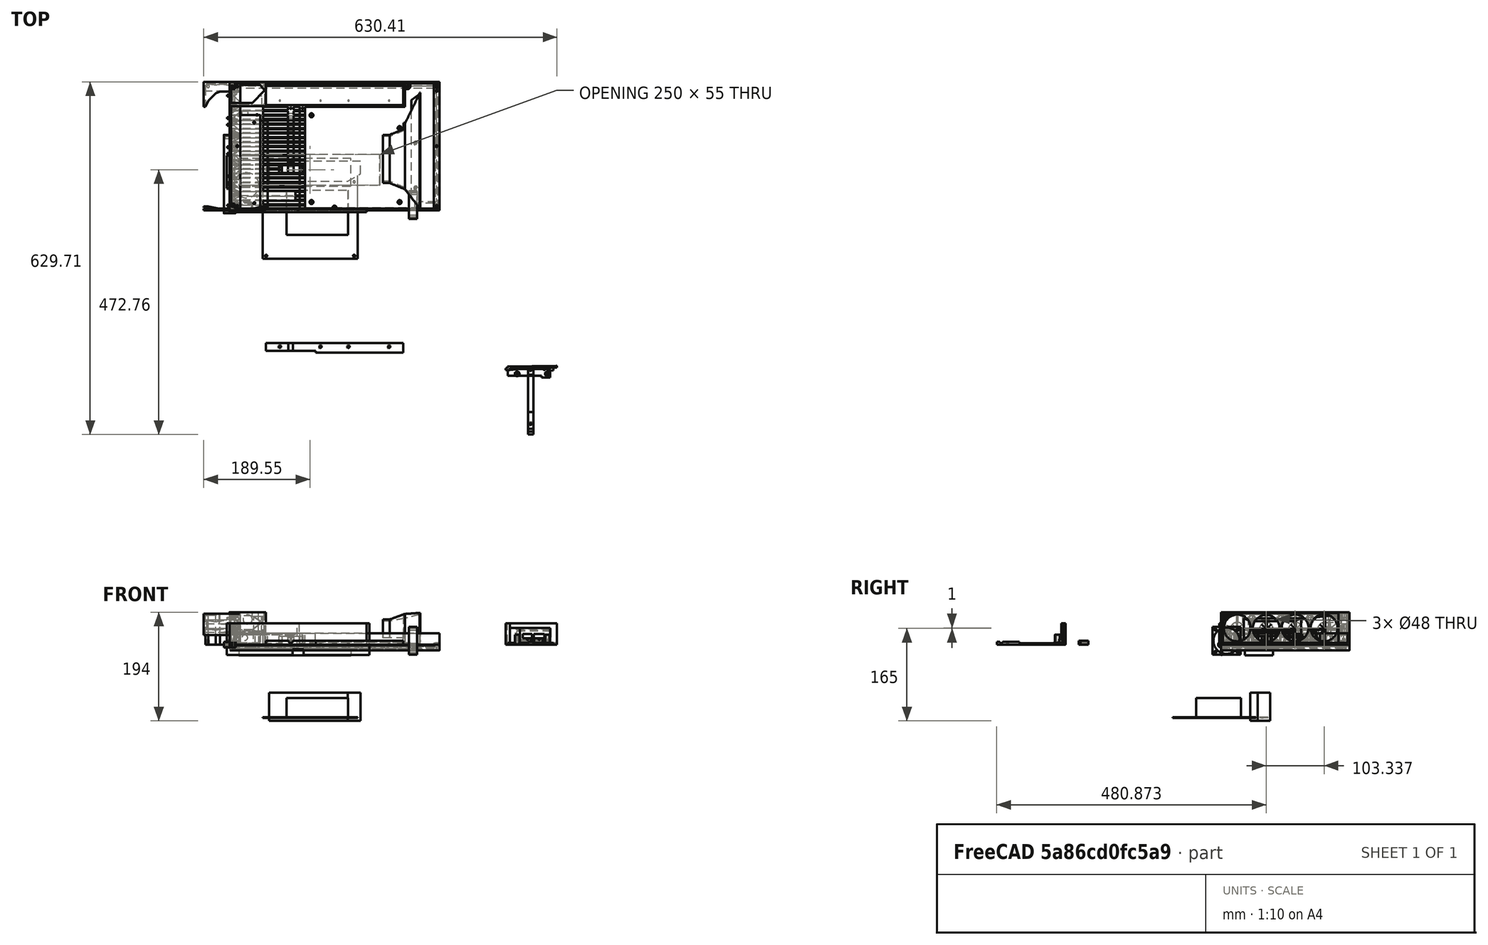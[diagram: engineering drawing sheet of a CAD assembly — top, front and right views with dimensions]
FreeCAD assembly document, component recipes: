
FREECAD ASSEMBLY — COMPONENT RECIPES ("4_fan_duct_version")

This assembly document has 13 components, labeled P0..P12 below (a component is one placed body or linked part). 13 of them carry a construction recipe — the FreeCAD feature program that regenerates the part from scratch, quoted from this document or its linked companion documents; the rest are supplied as boundary geometry only. No exploded tour is included for this assembly.
NOTE — this tour is split across 2 documents so each fits a 32k-token context. This is document 1: the component sections continue in the remaining 1 document, each repeating the header above.
COMPONENT P0 — recipe-attached ("BASE001", modeled in this document).
Construction recipe (the document's own serialized feature program — sketch geometry with constraints, then the solid features built on it; lengths are millimeters unless a unit is written):

FEATURE [Sketcher::SketchObject] Sketch014
  ArcFitTolerance = 1e-06
  AttachmentSupport = -> [XY_Plane013]
  FullyConstrained = true
  MakeInternals = false
  MapMode = 5
  expr: Constraints[20] = <<components>>.frame_w
  expr: Constraints[21] = <<components>>.frame_h
  expr: Constraints[22] = <<choices>>.corner
  expr: Constraints[25] = <<choices>>.shroud_base_screw_x
  expr: Constraints[26] = <<choices>>.shroud_base_screw_y2
  expr: Constraints[30] = <<choices>>.shroud_base_screw_y1
  expr: Constraints[31] = <<components>>.m3_threadhole
  expr: Constraints[33] = <<components>>.m3_hole
  expr: Constraints[34] = <<components>>.frame_w / 2
  sketch-geometry (14):
    g0: LineSegment StartX=1 StartY=0 StartZ=0 EndX=374 EndY=0 EndZ=0
    g1: LineSegment StartX=375 StartY=1 StartZ=0 EndX=375 EndY=228.5 EndZ=0
    g2: LineSegment StartX=374 StartY=229.5 StartZ=0 EndX=1 EndY=229.5 EndZ=0
    g3: LineSegment StartX=0 StartY=228.5 StartZ=0 EndX=0 EndY=1 EndZ=0
    g4: ArcOfCircle CenterX=1 CenterY=1 CenterZ=0 NormalX=0 NormalY=0 NormalZ=1 AngleXU=0 Radius=1 StartAngle=3.14159 EndAngle=4.71239
    g5: ArcOfCircle CenterX=374 CenterY=1 CenterZ=0 NormalX=0 NormalY=0 NormalZ=1 AngleXU=0 Radius=1 StartAngle=4.71239 EndAngle=6.28319
    g6: ArcOfCircle CenterX=374 CenterY=228.5 CenterZ=0 NormalX=0 NormalY=0 NormalZ=1 AngleXU=0 Radius=1 StartAngle=1.7e-15 EndAngle=1.5708
    g7: ArcOfCircle CenterX=1 CenterY=228.5 CenterZ=0 NormalX=0 NormalY=0 NormalZ=1 AngleXU=0 Radius=1 StartAngle=1.5708 EndAngle=3.14159
    g8: GeomPoint [constr] X=0 Y=0 Z=0
    g9: GeomPoint [constr] X=375 Y=229.5 Z=0
    g10: LineSegment [constr] StartX=332.5 StartY=0 StartZ=0 EndX=332.5 EndY=120 EndZ=0
    g11: Circle CenterX=332.5 CenterY=120 CenterZ=0 NormalX=0 NormalY=0 NormalZ=1 AngleXU=0 Radius=1.25
    g12: Circle CenterX=332.5 CenterY=40 CenterZ=0 NormalX=0 NormalY=0 NormalZ=1 AngleXU=0 Radius=1.25
    g13: Circle CenterX=187.5 CenterY=5 CenterZ=0 NormalX=0 NormalY=0 NormalZ=1 AngleXU=0 Radius=1.75
  constraints (35):
    c: Tangent(g0,g4) = -1.5708
    c: Tangent(g0,g5) = -1.5708
    c: Tangent(g1,g5) = -1.5708
    c: Tangent(g1,g6) = -1.5708
    c: Tangent(g2,g6) = -1.5708
    c: Tangent(g2,g7) = -1.5708
    c: Tangent(g3,g7) = -1.5708
    c: Tangent(g3,g4) = -1.5708
    c: Horizontal(g0)
    c: Horizontal(g2)
    c: Vertical(g1)
    c: Vertical(g3)
    c: Equal(g4,g5)
    c: Equal(g5,g6)
    c: Equal(g6,g7)
    c: PointOnObject(g8,g0)
    c: PointOnObject(g8,g3)
    c: PointOnObject(g9,g1)
    c: PointOnObject(g9,g2)
    c: Coincident(g8,g-1)
    c: DistanceX(g9) = 375
    c: DistanceY(g9) = 229.5
    c: Radius(g5) = 1
    c: PointOnObject(g10,g0)
    c: Vertical(g10)
    c: DistanceX(g10) = 332.5
    c: DistanceY(g10) = 120
    c: Coincident(g11,g10)
    c: PointOnObject(g12,g10)
    c: Equal(g12,g11)
    c: DistanceY(g12) = 40
    c: Diameter(g11) = 2.5
    c: DistanceY(g13) = 5
    c: Diameter(g13) = 3.5
    c: DistanceX(g13) = 187.5
FEATURE [PartDesign::Pad] Pad011
  Direction = (0,0,1)
  Length = 1.5
  Length2 = 10
  Profile = -> Sketch014
  ReferenceAxis = -> Sketch014 [N_Axis]
  Refine = true
  Suppressed = false
  Type = 0
FEATURE [Sketcher::SketchObject] Sketch016  label="motherboard standoffs"
  ArcFitTolerance = 1e-06
  AttachmentSupport = -> [XY_Plane013]
  FullyConstrained = false
  MakeInternals = false
  MapMode = 5
  expr: Constraints[10] = <<components>>.frame_w
  expr: Constraints[21] = <<choices>>.shroud_mb_space + <<components>>.fan_w + <<choices>>.exit_w
  expr: Constraints[42] = <<components>>.m3_threadhole
  expr: Constraints[51] = <<choices>>.mb_front_edge_gap
  expr: Constraints[57] = <<components>>.frame_w / 2
  expr: Constraints[62] = <<choices>>.screwhole_edge_margin
  expr: Constraints[63] = <<components>>.m3_hole
  expr: Constraints[9] = <<components>>.frame_h
  sketch-geometry (25):
    g0: LineSegment [constr] StartX=0 StartY=0 StartZ=0 EndX=375 EndY=0 EndZ=0
    g1: LineSegment [constr] StartX=375 StartY=0 StartZ=0 EndX=375 EndY=229.5 EndZ=0
    g2: LineSegment [constr] StartX=375 StartY=229.5 StartZ=0 EndX=0 EndY=229.5 EndZ=0
    g3: LineSegment [constr] StartX=0 StartY=229.5 StartZ=0 EndX=0 EndY=0 EndZ=0
    g4: LineSegment [constr] StartX=140 StartY=180 StartZ=0 EndX=140 EndY=10 EndZ=0
    g5: LineSegment [constr] StartX=140 StartY=10 StartZ=0 EndX=310 EndY=10 EndZ=0
    g6: LineSegment [constr] StartX=310 StartY=10 StartZ=0 EndX=310 EndY=180 EndZ=0
    g7: LineSegment [constr] StartX=310 StartY=180 StartZ=0 EndX=140 EndY=180 EndZ=0
    g8: LineSegment [constr] StartX=146.35 StartY=169.84 StartZ=0 EndX=146.35 EndY=14.8997 EndZ=0
    g9: LineSegment [constr] StartX=146.35 StartY=14.8997 StartZ=0 EndX=303.65 EndY=14.8997 EndZ=0
    g10: LineSegment [constr] StartX=303.65 StartY=14.8997 StartZ=0 EndX=303.65 EndY=146.98 EndZ=0
    g11: LineSegment [constr] StartX=303.65 StartY=146.98 StartZ=0 EndX=146.35 EndY=146.98 EndZ=0
    g12: Circle CenterX=146.35 CenterY=169.84 CenterZ=0 NormalX=0 NormalY=0 NormalZ=1 AngleXU=0 Radius=1.25
    g13: Circle CenterX=303.65 CenterY=146.98 CenterZ=0 NormalX=0 NormalY=0 NormalZ=1 AngleXU=0 Radius=1.25
    g14: Circle CenterX=303.65 CenterY=14.8997 CenterZ=0 NormalX=0 NormalY=0 NormalZ=1 AngleXU=0 Radius=1.25
    g15: Circle CenterX=146.35 CenterY=14.8997 CenterZ=0 NormalX=0 NormalY=0 NormalZ=1 AngleXU=0 Radius=1.25
    g16: Circle CenterX=146.35 CenterY=169.84 CenterZ=0 NormalX=0 NormalY=0 NormalZ=1 AngleXU=0 Radius=3.5
    g17: Circle CenterX=303.65 CenterY=146.98 CenterZ=0 NormalX=0 NormalY=0 NormalZ=1 AngleXU=0 Radius=3.5
    g18: Circle CenterX=303.65 CenterY=14.8997 CenterZ=0 NormalX=0 NormalY=0 NormalZ=1 AngleXU=0 Radius=3.5
    g19: Circle CenterX=146.35 CenterY=14.8997 CenterZ=0 NormalX=0 NormalY=0 NormalZ=1 AngleXU=0 Radius=3.5
    g20: Circle CenterX=187.5 CenterY=5 CenterZ=0 NormalX=0 NormalY=0 NormalZ=1 AngleXU=0 Radius=1.75
    g21: ArcOfCircle CenterX=187.5 CenterY=5 CenterZ=0 NormalX=0 NormalY=0 NormalZ=1 AngleXU=0 Radius=3.5 StartAngle=2e-16 EndAngle=3.14609
    g22: LineSegment StartX=191 StartY=5 StartZ=0 EndX=191 EndY=0 EndZ=0
    g23: LineSegment StartX=184 StartY=4.98426 StartZ=0 EndX=184.022 EndY=0 EndZ=0
    g24: LineSegment StartX=184.022 StartY=0 StartZ=0 EndX=191 EndY=0 EndZ=0
  constraints (64):
    c: Coincident(g0,g1)
    c: Coincident(g1,g2)
    c: Coincident(g2,g3)
    c: Coincident(g3,g0)
    c: Horizontal(g0)
    c: Horizontal(g2)
    c: Vertical(g1)
    c: Vertical(g3)
    c: Coincident(g0,g-1)
    c: DistanceY(g1,g1) = 229.5
    c: DistanceX(g2,g2) = 375
    c: Coincident(g4,g5)
    c: Coincident(g5,g6)
    c: Coincident(g6,g7)
    c: Coincident(g7,g4)
    c: Vertical(g4)
    c: Vertical(g6)
    c: Horizontal(g5)
    c: Horizontal(g7)
    c: Distance(g4,g6) = 170
    c: Distance(g5,g7) = 170
    c: Distance(g5,g1) = 65
    c: Vertical(g8)
    c: Coincident(g8,g9)
    c: Horizontal(g9)
    c: Coincident(g9,g10)
    c: Vertical(g10)
    c: Coincident(g10,g11)
    c: PointOnObject(g11,g8)
    c: Horizontal(g11)
    c: Distance(g8,g5) = 4.8997
    c: Distance(g8,g4) = 6.35
    c: Distance(g9,g6) = 6.35
    c: Distance(g8,g7) = 10.16
    c: Distance(g8,g11) = 22.86
    c: Coincident(g12,g8)
    c: Coincident(g13,g10)
    c: Coincident(g14,g9)
    c: Coincident(g15,g8)
    c: Equal(g12,g15)
    c: Equal(g15,g13)
    c: Equal(g13,g14)
    c: Diameter(g12) = 2.5
    c: Diameter(g16) = 7
    c: Coincident(g16,g8)
    c: Coincident(g17,g10)
    c: Coincident(g18,g9)
    c: Coincident(g19,g8)
    c: Equal(g18,g19)
    c: Equal(g19,g17)
    c: Equal(g17,g16)
    c: Distance(g4,g0) = 10
    c: Tangent(g21,g22) = 1.5708
    c: Tangent(g21,g23) = -1.5708
    c: Coincident(g21,g20)
    c: Vertical(g22)
    c: Equal(g19,g21)
    c: DistanceX(g20) = 187.5
    c: Coincident(g24,g23)
    c: Coincident(g24,g22)
    c: Horizontal(g24)
    c: PointOnObject(g23,g0)
    c: DistanceY(g20) = 5
    c: Diameter(g20) = 3.5
FEATURE [PartDesign::Pad] Pad013  label="mb_standoffs"
  BaseFeature = -> Pad011
  Direction = (0,0,1)
  Length = 7.25
  Length2 = 10
  Profile = -> Sketch016
  ReferenceAxis = -> Sketch016 [N_Axis]
  Refine = true
  Suppressed = false
  Type = 0
  expr: Length = <<choices>>.base_under_mb_thickness + 6
FEATURE [Sketcher::SketchObject] Sketch017
  ArcFitTolerance = 1e-06
  AttachmentSupport = -> [XY_Plane013]
  FullyConstrained = false
  MakeInternals = false
  MapMode = 5
  expr: Constraints[121] = <<choices>>.corner
  expr: Constraints[17] = <<components>>.fan_w + <<choices>>.exit_w + <<choices>>.shroud_mb_space + <<components>>.mb_w + 5
  expr: Constraints[31] = <<components>>.frame_h
  expr: Constraints[37] = <<choices>>.corner
  expr: Constraints[45] = <<choices>>.corner
  expr: Constraints[8] = <<components>>.frame_w
  expr: Constraints[9] = <<choices>>.mb_front_edge_gap + 170 + 5 + 3
  sketch-geometry (57):
    g0: LineSegment [constr] StartX=0 StartY=0 StartZ=0 EndX=375 EndY=0 EndZ=0
    g1: LineSegment [constr] StartX=375 StartY=0 StartZ=0 EndX=375 EndY=188 EndZ=0
    g2: LineSegment [constr] StartX=375 StartY=188 StartZ=0 EndX=0 EndY=188 EndZ=0
    g3: LineSegment [constr] StartX=0 StartY=188 StartZ=0 EndX=0 EndY=0 EndZ=0
    g4: LineSegment StartX=1 StartY=0 StartZ=0 EndX=374 EndY=0 EndZ=0
    g5: LineSegment StartX=375 StartY=1 StartZ=0 EndX=375 EndY=3 EndZ=0
    g6: LineSegment StartX=375 StartY=3 StartZ=0 EndX=135 EndY=3 EndZ=0
    g7: ArcOfCircle CenterX=1 CenterY=1 CenterZ=0 NormalX=0 NormalY=0 NormalZ=1 AngleXU=0 Radius=1 StartAngle=3.14159 EndAngle=4.71239
    g8: GeomPoint [constr] X=0 Y=0 Z=0
    g9: GeomPoint [constr] X=0 Y=188 Z=0
    g10: ArcOfCircle CenterX=374 CenterY=1 CenterZ=0 NormalX=0 NormalY=0 NormalZ=1 AngleXU=0 Radius=1 StartAngle=4.71239 EndAngle=6.28319
    g11: GeomPoint [constr] X=375 Y=0 Z=0
    g12: LineSegment StartX=375 StartY=228.5 StartZ=0 EndX=375 EndY=226.5 EndZ=0
    g13: LineSegment [constr] StartX=2 StartY=221.5 StartZ=0 EndX=2 EndY=192.907 EndZ=0
    g14: ArcOfCircle CenterX=1 CenterY=228.5 CenterZ=0 NormalX=0 NormalY=0 NormalZ=1 AngleXU=0 Radius=1 StartAngle=1.5708 EndAngle=3.14159
    g15: GeomPoint [constr] X=0 Y=229.5 Z=0
    g16: ArcOfCircle [constr] CenterX=7 CenterY=221.5 CenterZ=0 NormalX=0 NormalY=0 NormalZ=1 AngleXU=0 Radius=5 StartAngle=1.5708 EndAngle=3.14159
    g17: GeomPoint [constr] X=2 Y=226.5 Z=0
    g18: ArcOfCircle CenterX=374 CenterY=228.5 CenterZ=0 NormalX=0 NormalY=0 NormalZ=1 AngleXU=0 Radius=1 StartAngle=5.5e-15 EndAngle=1.5708
    g19: GeomPoint [constr] X=375 Y=229.5 Z=0
    g20: ArcOfCircle [constr] CenterX=7 CenterY=192.907 CenterZ=0 NormalX=0 NormalY=0 NormalZ=1 AngleXU=0 Radius=5 StartAngle=3.14159 EndAngle=4.90523
    g21: GeomPoint [constr] X=2 Y=188 Z=0
    g22: LineSegment StartX=313 StartY=226.5 StartZ=0 EndX=313 EndY=185 EndZ=0
    g23: LineSegment StartX=313 StartY=185 StartZ=0 EndX=310 EndY=185 EndZ=0
    g24: LineSegment StartX=310 StartY=185 StartZ=0 EndX=310 EndY=226.5 EndZ=0
    g25: LineSegment StartX=375 StartY=226.5 StartZ=0 EndX=313 EndY=226.5 EndZ=0
    g26: LineSegment [constr] StartX=313 StartY=226.5 StartZ=0 EndX=310 EndY=226.5 EndZ=0
    g27: LineSegment StartX=1 StartY=229.5 StartZ=0 EndX=308.406 EndY=229.5 EndZ=0
    g28: LineSegment [constr] StartX=308.406 StartY=229.5 StartZ=0 EndX=310 EndY=229.5 EndZ=0
    g29: LineSegment StartX=310 StartY=229.5 StartZ=0 EndX=374 EndY=229.5 EndZ=0
    g30: LineSegment [constr] StartX=310 StartY=226.5 StartZ=0 EndX=307.803 EndY=226.5 EndZ=0
    g31: LineSegment StartX=308.406 StartY=229.5 StartZ=0 EndX=307.803 EndY=226.5 EndZ=0
    g32: LineSegment StartX=310 StartY=229.5 StartZ=0 EndX=310 EndY=226.5 EndZ=0
    g33: LineSegment StartX=58 StartY=226.5 StartZ=0 EndX=7 EndY=226.5 EndZ=0
    g34: LineSegment StartX=307.803 StartY=226.5 StartZ=0 EndX=65 EndY=226.5 EndZ=0
    g35: LineSegment [constr] StartX=65 StartY=226.5 StartZ=0 EndX=63 EndY=226.5 EndZ=0
    g36: LineSegment StartX=58 StartY=188 StartZ=0 EndX=7.95824 EndY=188 EndZ=0
    g37: LineSegment StartX=135 StartY=188 StartZ=0 EndX=65 EndY=188 EndZ=0
    g38: LineSegment [constr] StartX=65 StartY=188 StartZ=0 EndX=63 EndY=188 EndZ=0
    g39: LineSegment StartX=63 StartY=221.5 StartZ=0 EndX=63 EndY=193 EndZ=0
    g40: LineSegment StartX=65 StartY=188 StartZ=0 EndX=65 EndY=226.5 EndZ=0
    g41: ArcOfCircle CenterX=58 CenterY=193 CenterZ=0 NormalX=0 NormalY=0 NormalZ=1 AngleXU=0 Radius=5 StartAngle=4.71239 EndAngle=6.28319
    g42: GeomPoint [constr] X=63 Y=188 Z=0
    g43: ArcOfCircle CenterX=58 CenterY=221.5 CenterZ=0 NormalX=0 NormalY=0 NormalZ=1 AngleXU=0 Radius=5 StartAngle=1.3e-15 EndAngle=1.5708
    g44: GeomPoint [constr] X=63 Y=226.5 Z=0
    g45: LineSegment StartX=135 StartY=3 StartZ=0 EndX=135 EndY=185 EndZ=0
    g46: LineSegment [constr] StartX=135 StartY=185 StartZ=0 EndX=135 EndY=188 EndZ=0
    g47: LineSegment StartX=135 StartY=188 StartZ=0 EndX=152 EndY=188 EndZ=0
    g48: LineSegment StartX=153 StartY=187 StartZ=0 EndX=153 EndY=185 EndZ=0
    g49: LineSegment StartX=153 StartY=185 StartZ=0 EndX=135 EndY=185 EndZ=0
    g50: ArcOfCircle CenterX=152 CenterY=187 CenterZ=0 NormalX=0 NormalY=0 NormalZ=1 AngleXU=0 Radius=1 StartAngle=1e-14 EndAngle=1.5708
    g51: GeomPoint [constr] X=153 Y=188 Z=0
    g52: LineSegment StartX=0 StartY=228.5 StartZ=0 EndX=0 EndY=226.5 EndZ=0
    g53: LineSegment [constr] StartX=0 StartY=226.5 StartZ=0 EndX=0 EndY=188 EndZ=0
    g54: LineSegment StartX=0 StartY=188 StartZ=0 EndX=-6e-16 EndY=1 EndZ=0
    g55: LineSegment StartX=0 StartY=226.5 StartZ=0 EndX=7 EndY=226.5 EndZ=0
    g56: LineSegment StartX=0 StartY=188 StartZ=0 EndX=7.95824 EndY=188 EndZ=0
  constraints (135):
    c: Coincident(g0,g1)
    c: Coincident(g2,g3)
    c: Coincident(g3,g0)
    c: Horizontal(g0)
    c: Horizontal(g2)
    c: Vertical(g1)
    c: Vertical(g3)
    c: Coincident(g0,g-1)
    c: DistanceX(g2,g2) = 375
    c: DistanceY(g1,g1) = 188
    c: Coincident(g9,g2)
    c: Coincident(g8,g0)
    c: Coincident(g11,g0)
    c: PointOnObject(g5,g1)
    c: Coincident(g5,g6)
    c: Horizontal(g6)
    c: Coincident(g6,g45)
    c: Distance(g6,g1) = 240
    c: PointOnObject(g8,g4)
    c: Tangent(g4,g7) = -1.5708
    c: Coincident(g54,g7) = -1.5708
    c: PointOnObject(g11,g5)
    c: PointOnObject(g11,g4)
    c: Tangent(g5,g10) = -1.5708
    c: Tangent(g4,g10) = -1.5708
    c: PointOnObject(g46,g2)
    c: Coincident(g37,g46)
    c: Radius(g10) = 1
    c: Coincident(g2,g1)
    c: DistanceY(g6) = 3
    c: DistanceX(g21) = 2
    c: DistanceY(g15) = 229.5
    c: Coincident(g12,g25)
    c: Vertical(g13)
    c: Coincident(g52,g14) = -1.5708
    c: Coincident(g27,g14) = 1.5708
    c: Equal(g14,g7)
    c: Radius(g7) = 1
    c: PointOnObject(g17,g13)
    c: Tangent(g13,g16) = -1.5708
    c: Vertical(g12)
    c: PointOnObject(g12,g1)
    c: PointOnObject(g19,g12)
    c: Coincident(g29,g18) = 1.5708
    c: Tangent(g12,g18) = 1.5708
    c: Radius(g18) = 1
    c: PointOnObject(g21,g13)
    c: Coincident(g36,g20) = 1.5708
    c: Tangent(g13,g20) = -1.5708
    c: Equal(g20,g16)
    c: Radius(g16) = 5
    c: Vertical(g22)
    c: Coincident(g22,g23)
    c: Horizontal(g23)
    c: Coincident(g23,g24)
    c: Vertical(g24)
    c: Coincident(g26,g30)
    c: Coincident(g25,g26)
    c: Horizontal(g25)
    c: Horizontal(g26)
    c: PointOnObject(g17,g25)
    c: Coincident(g25,g22)
    c: Coincident(g30,g24)
    c: Distance(g22,g1) = 62
    c: Distance(g46,g23) = 3
    c: DistanceX(g23,g23) = 3
    c: Coincident(g27,g28)
    c: Horizontal(g27)
    c: Distance(g17,g27) = 3
    c: PointOnObject(g15,g27)
    c: PointOnObject(g19,g27)
    c: Coincident(g28,g29)
    c: Horizontal(g28)
    c: Horizontal(g29)
    c: Coincident(g30,g34)
    c: Horizontal(g30)
    c: Coincident(g31,g27)
    c: Coincident(g31,g30)
    c: Coincident(g32,g28)
    c: Coincident(g32,g24)
    c: Vertical(g32)
    c: Coincident(g35,g44)
    c: Horizontal(g33)
    c: Coincident(g34,g35)
    c: Horizontal(g34)
    c: Horizontal(g35)
    c: Coincident(g38,g42)
    c: Horizontal(g36)
    c: Coincident(g37,g38)
    c: Horizontal(g37)
    c: Horizontal(g38)
    c: PointOnObject(g21,g37)
    c: Vertical(g39)
    c: Coincident(g40,g37)
    c: Coincident(g40,g34)
    c: Vertical(g40)
    c: Distance(g42,g40) = 2
    c: DistanceX(g34) = 65
    c: PointOnObject(g42,g36)
    c: PointOnObject(g42,g39)
    c: Tangent(g36,g41) = 1.5708
    c: Tangent(g39,g41) = 1.5708
    c: PointOnObject(g44,g39)
    c: Tangent(g39,g43) = 1.5708
    c: Equal(g16,g43)
    c: Equal(g43,g41)
    c: Coincident(g45,g46)
    c: Vertical(g45)
    c: Vertical(g46)
    c: Coincident(g37,g47)
    c: PointOnObject(g51,g2)
    c: Vertical(g48)
    c: Coincident(g48,g49)
    c: Coincident(g49,g45)
    c: Horizontal(g49)
    c: DistanceY(g48,g51) = 3
    c: DistanceX(g47,g51) = 18
    c: PointOnObject(g51,g47)
    c: PointOnObject(g51,g48)
    c: Tangent(g47,g50) = 1.5708
    c: Tangent(g48,g50) = 1.5708
    c: Radius(g50) = 1
    c: Tangent(g43,g33) = -1.5708
    c: Tangent(g16,g33) = -1.5708
    c: Distance(g16,g27) = 3
    c: Coincident(g52,g53)
    c: PointOnObject(g8,g52)
    c: PointOnObject(g9,g52)
    c: PointOnObject(g15,g52)
    c: Coincident(g53,g54)
    c: Coincident(g55,g52)
    c: Tangent(g55,g16) = 1.5708
    c: Coincident(g56,g53)
    c: Coincident(g56,g20)
    c: Horizontal(g56)
FEATURE [PartDesign::Pad] Pad014  label="thick_area"
  BaseFeature = -> Pad013
  Direction = (0,0,1)
  Length = 20
  Length2 = 10
  Profile = -> Sketch017
  ReferenceAxis = -> Sketch017 [N_Axis]
  Refine = true
  Suppressed = false
  Type = 0
  expr: Length = <<choices>>.base_max_thickness
FEATURE [Sketcher::SketchObject] Sketch018
  ArcFitTolerance = 1e-06
  AttachmentSupport = -> [XY_Plane013]
  FullyConstrained = true
  MakeInternals = false
  MapMode = 5
  expr: Constraints[30] = <<components>>.m3_hole
  expr: Constraints[31] = <<choices>>.psu_left_gap
  sketch-geometry (14):
    g0: LineSegment [constr] StartX=60 StartY=183 StartZ=0 EndX=5 EndY=183 EndZ=0
    g1: LineSegment [constr] StartX=5 StartY=183 StartZ=0 EndX=5 EndY=13 EndZ=0
    g2: LineSegment [constr] StartX=5 StartY=13 StartZ=0 EndX=60 EndY=13 EndZ=0
    g3: LineSegment [constr] StartX=60 StartY=13 StartZ=0 EndX=60 EndY=183 EndZ=0
    g4: GeomPoint [constr] X=32.5 Y=98 Z=0
    g5: LineSegment [constr] StartX=49.15 StartY=170 StartZ=0 EndX=15.85 EndY=170 EndZ=0
    g6: LineSegment [constr] StartX=15.85 StartY=170 StartZ=0 EndX=15.85 EndY=26 EndZ=0
    g7: LineSegment [constr] StartX=15.85 StartY=26 StartZ=0 EndX=49.15 EndY=26 EndZ=0
    g8: LineSegment [constr] StartX=49.15 StartY=26 StartZ=0 EndX=49.15 EndY=170 EndZ=0
    g9: GeomPoint [constr] X=32.5 Y=98 Z=0
    g10: Circle CenterX=15.85 CenterY=170 CenterZ=0 NormalX=0 NormalY=0 NormalZ=1 AngleXU=0 Radius=1.75
    g11: Circle CenterX=49.15 CenterY=170 CenterZ=0 NormalX=0 NormalY=0 NormalZ=1 AngleXU=0 Radius=1.75
    g12: Circle CenterX=15.85 CenterY=26 CenterZ=0 NormalX=0 NormalY=0 NormalZ=1 AngleXU=0 Radius=1.75
    g13: Circle CenterX=49.15 CenterY=26 CenterZ=0 NormalX=0 NormalY=0 NormalZ=1 AngleXU=0 Radius=1.75
  constraints (33):
    c: Coincident(g0,g1)
    c: Coincident(g1,g2)
    c: Coincident(g2,g3)
    c: Coincident(g3,g0)
    c: Horizontal(g0)
    c: Horizontal(g2)
    c: Vertical(g1)
    c: Vertical(g3)
    c: Symmetric(g2,g0,g4)
    c: Coincident(g5,g6)
    c: Coincident(g6,g7)
    c: Coincident(g7,g8)
    c: Coincident(g8,g5)
    c: Horizontal(g5)
    c: Horizontal(g7)
    c: Vertical(g6)
    c: Vertical(g8)
    c: Symmetric(g7,g5,g9)
    c: Coincident(g9,g4)
    c: DistanceX(g5,g5) = 33.3
    c: DistanceY(g6,g6) = 144
    c: DistanceY(g1,g1) = 170
    c: DistanceX(g0,g0) = 55
    c: Coincident(g10,g5)
    c: Coincident(g11,g5)
    c: Coincident(g12,g6)
    c: Coincident(g13,g7)
    c: Equal(g10,g11)
    c: Equal(g11,g12)
    c: Equal(g12,g13)
    c: Diameter(g10) = 3.5
    c: DistanceX(g-2,g1) = 5
    c: DistanceY(g1) = 13
FEATURE [PartDesign::Pocket] Pocket004  label="psu_mounts"
  BaseFeature = -> Pad014
  Direction = (0,0,-1)
  Length = 5
  Length2 = 5
  Profile = -> Sketch018
  ReferenceAxis = -> Sketch018 [N_Axis]
  Refine = true
  Reversed = true
  Suppressed = false
  Type = 1
FEATURE [Sketcher::SketchObject] Sketch019
  ArcFitTolerance = 1e-06
  AttachmentSupport = -> [XY_Plane013]
  FullyConstrained = true
  MakeInternals = false
  MapMode = 5
  expr: Constraints[10] = <<components>>.frame_h
  expr: Constraints[20] = <<choices>>.mb_front_edge_gap + 170 + 5 + 3
  expr: Constraints[21] = <<choices>>.exit_w + <<components>>.fan_w + <<choices>>.shroud_mb_space
  expr: Constraints[9] = <<components>>.frame_w
  sketch-geometry (8):
    g0: LineSegment [constr] StartX=0 StartY=0 StartZ=0 EndX=375 EndY=0 EndZ=0
    g1: LineSegment [constr] StartX=375 StartY=0 StartZ=0 EndX=375 EndY=229.5 EndZ=0
    g2: LineSegment [constr] StartX=375 StartY=229.5 StartZ=0 EndX=0 EndY=229.5 EndZ=0
    g3: LineSegment [constr] StartX=0 StartY=229.5 StartZ=0 EndX=0 EndY=0 EndZ=0
    g4: LineSegment StartX=65 StartY=188 StartZ=0 EndX=310 EndY=188 EndZ=0
    g5: LineSegment StartX=310 StartY=188 StartZ=0 EndX=310 EndY=229.5 EndZ=0
    g6: LineSegment StartX=310 StartY=229.5 StartZ=0 EndX=65 EndY=229.5 EndZ=0
    g7: LineSegment StartX=65 StartY=229.5 StartZ=0 EndX=65 EndY=188 EndZ=0
  constraints (23):
    c: Coincident(g0,g1)
    c: Coincident(g1,g2)
    c: Coincident(g2,g3)
    c: Coincident(g3,g0)
    c: Horizontal(g0)
    c: Horizontal(g2)
    c: Vertical(g1)
    c: Vertical(g3)
    c: Coincident(g0,g-1)
    c: DistanceX(g2,g2) = 375
    c: DistanceY(g1,g1) = 229.5
    c: Coincident(g4,g5)
    c: Coincident(g5,g6)
    c: Coincident(g6,g7)
    c: Coincident(g7,g4)
    c: Horizontal(g4)
    c: Horizontal(g6)
    c: Vertical(g5)
    c: Vertical(g7)
    c: PointOnObject(g5,g2)
    c: Distance(g4,g0) = 188
    c: Distance(g4,g1) = 65
    c: DistanceX(g6) = 65
FEATURE [PartDesign::Pocket] Pocket005  label="back_hole"
  BaseFeature = -> Pocket004
  Direction = (0,0,-1)
  Length = 5
  Length2 = 5
  Profile = -> Sketch019
  ReferenceAxis = -> Sketch019 [N_Axis]
  Refine = true
  Reversed = true
  Suppressed = false
  Type = 1
FEATURE [Sketcher::SketchObject] Sketch020
  ArcFitTolerance = 1e-06
  AttachmentSupport = -> [XY_Plane013]
  FullyConstrained = false
  MakeInternals = false
  MapMode = 5
  expr: Constraints[20] = <<choices>>.fin_gap
  expr: Constraints[21] = <<choices>>.fin_end
  expr: Constraints[9] = <<components>>.frame_h
  sketch-geometry (8):
    g0: LineSegment [constr] StartX=0 StartY=0 StartZ=0 EndX=125.373 EndY=0 EndZ=0
    g1: LineSegment [constr] StartX=125.373 StartY=0 StartZ=0 EndX=125.373 EndY=229.5 EndZ=0
    g2: LineSegment [constr] StartX=125.373 StartY=229.5 StartZ=0 EndX=0 EndY=229.5 EndZ=0
    g3: LineSegment [constr] StartX=0 StartY=229.5 StartZ=0 EndX=0 EndY=0 EndZ=0
    g4: LineSegment StartX=0 StartY=3 StartZ=0 EndX=125.373 EndY=3 EndZ=0
    g5: LineSegment StartX=125.373 StartY=3 StartZ=0 EndX=125.373 EndY=9 EndZ=0
    g6: LineSegment StartX=125.373 StartY=9 StartZ=0 EndX=0 EndY=9 EndZ=0
    g7: LineSegment StartX=0 StartY=9 StartZ=0 EndX=0 EndY=3 EndZ=0
  constraints (22):
    c: Coincident(g0,g1)
    c: Coincident(g1,g2)
    c: Coincident(g2,g3)
    c: Coincident(g3,g0)
    c: Horizontal(g0)
    c: Horizontal(g2)
    c: Vertical(g1)
    c: Vertical(g3)
    c: Coincident(g0,g-1)
    c: DistanceY(g1,g1) = 229.5
    c: Coincident(g4,g5)
    c: Coincident(g5,g6)
    c: Coincident(g6,g7)
    c: Coincident(g7,g4)
    c: Horizontal(g4)
    c: Horizontal(g6)
    c: Vertical(g5)
    c: Vertical(g7)
    c: PointOnObject(g4,g3)
    c: PointOnObject(g5,g1)
    c: DistanceY(g5,g5) = 6
    c: Distance(g4,g0) = 3
FEATURE [PartDesign::Pocket] Pocket006
  BaseFeature = -> Pocket005
  Direction = (0,0,-1)
  Length = 18
  Length2 = 5
  Profile = -> Sketch020
  ReferenceAxis = -> Sketch020 [N_Axis]
  Refine = true
  Reversed = true
  Suppressed = false
  Type = 0
  expr: Length = <<choices>>.base_max_thickness - 2
FEATURE [PartDesign::Plane] DatumPlane001  label="just_above_base_thinnest"
  AttachmentOffset = pos=(0,0,2) rot=(0,0,1;0rad)
  AttachmentSupport = -> [XY_Plane013]
  Length = 463.812
  MapMode = 5
  Placement = pos=(0,0,2) rot=(0,0,1;0rad)
  ResizeMode = 0
  Width = 318.312
FEATURE [Sketcher::SketchObject] Sketch021
  ArcFitTolerance = 1e-06
  AttachmentSupport = -> [DatumPlane001]
  FullyConstrained = true
  MakeInternals = false
  MapMode = 5
  Placement = pos=(0,0,2) rot=(0,0,1;0rad)
  expr: Constraints[19] = <<choices>>.fin_gap
  expr: Constraints[20] = <<choices>>.fin_end
  expr: Constraints[21] = <<choices>>.psu_left_gap + <<components>>.psu_w
  expr: Constraints[22] = <<components>>.frame_w - <<components>>.fan_w - <<choices>>.exit_w - <<choices>>.shroud_mb_space - 170 - 5
  expr: Constraints[9] = <<components>>.frame_h
  sketch-geometry (8):
    g0: LineSegment [constr] StartX=0 StartY=0 StartZ=0 EndX=135 EndY=0 EndZ=0
    g1: LineSegment [constr] StartX=135 StartY=0 StartZ=0 EndX=135 EndY=229.5 EndZ=0
    g2: LineSegment [constr] StartX=135 StartY=229.5 StartZ=0 EndX=0 EndY=229.5 EndZ=0
    g3: LineSegment [constr] StartX=0 StartY=229.5 StartZ=0 EndX=0 EndY=0 EndZ=0
    g4: LineSegment StartX=60 StartY=3 StartZ=0 EndX=135 EndY=3 EndZ=0
    g5: LineSegment StartX=135 StartY=3 StartZ=0 EndX=135 EndY=9 EndZ=0
    g6: LineSegment StartX=135 StartY=9 StartZ=0 EndX=60 EndY=9 EndZ=0
    g7: LineSegment StartX=60 StartY=9 StartZ=0 EndX=60 EndY=3 EndZ=0
  constraints (23):
    c: Coincident(g0,g1)
    c: Coincident(g1,g2)
    c: Coincident(g2,g3)
    c: Coincident(g3,g0)
    c: Horizontal(g0)
    c: Horizontal(g2)
    c: Vertical(g1)
    c: Vertical(g3)
    c: Coincident(g0,g-1)
    c: DistanceY(g1,g1) = 229.5
    c: Coincident(g4,g5)
    c: Coincident(g5,g6)
    c: Coincident(g6,g7)
    c: Coincident(g7,g4)
    c: Horizontal(g4)
    c: Horizontal(g6)
    c: Vertical(g5)
    c: Vertical(g7)
    c: PointOnObject(g5,g1)
    c: DistanceY(g5,g5) = 6
    c: Distance(g4,g0) = 3
    c: Distance(g4,g3) = 60
    c: DistanceX(g0) = 135
FEATURE [PartDesign::Pocket] Pocket007
  BaseFeature = -> Pocket006
  Direction = (0,0,-1)
  Length = 5
  Length2 = 5
  Profile = -> Sketch021
  ReferenceAxis = -> Sketch021 [N_Axis]
  Refine = true
  Reversed = true
  Suppressed = false
  Type = 1
FEATURE [PartDesign::LinearPattern] LinearPattern
  BaseFeature = -> Pocket007
  Direction = -> Sketch020 [V_Axis]
  Length = 176
  Mode = 1
  Occurrences = 23
  Offset = 8
  Originals = -> [Pocket006,Pocket007]
  Refine = true
  Suppressed = false
  TransformMode = 0
  expr: Occurrences = <<choices>>.fin_count + 1
  expr: Offset = <<choices>>.fin_thick + <<choices>>.fin_gap
FEATURE [Sketcher::SketchObject] Sketch035
  ArcFitTolerance = 1e-06
  AttachmentSupport = -> [XY_Plane013]
  FullyConstrained = false
  MakeInternals = false
  MapMode = 5
  expr: Constraints[10] = <<components>>.frame_w - 62
  expr: Constraints[8] = 170 + <<choices>>.mb_front_edge_gap + 5 + 3
  sketch-geometry (4):
    g0: LineSegment StartX=127.279 StartY=188 StartZ=0 EndX=127.279 EndY=185 EndZ=0
    g1: LineSegment StartX=127.279 StartY=185 StartZ=0 EndX=313 EndY=185 EndZ=0
    g2: LineSegment StartX=313 StartY=185 StartZ=0 EndX=313 EndY=188 EndZ=0
    g3: LineSegment StartX=313 StartY=188 StartZ=0 EndX=127.279 EndY=188 EndZ=0
  constraints (11):
    c: Coincident(g0,g1)
    c: Coincident(g1,g2)
    c: Coincident(g2,g3)
    c: Coincident(g3,g0)
    c: Vertical(g0)
    c: Vertical(g2)
    c: Horizontal(g1)
    c: Horizontal(g3)
    c: DistanceY(g0) = 188
    c: DistanceY(g0,g0) = 3
    c: DistanceX(g2) = 313
FEATURE [PartDesign::Pad] Pad020  label="lip in front of rear ports"
  BaseFeature = -> LinearPattern
  Direction = (0,0,1)
  Length = 4.25
  Length2 = 10
  Profile = -> Sketch035
  ReferenceAxis = -> Sketch035 [N_Axis]
  Refine = true
  Suppressed = false
  Type = 0
  expr: Length = 3 + <<choices>>.base_under_mb_thickness
FEATURE [Sketcher::SketchObject] Sketch045
  ArcFitTolerance = 1e-06
  AttachmentSupport = -> [XY_Plane013]
  FullyConstrained = false
  MakeInternals = false
  MapMode = 5
  expr: Constraints[19] = <<choices>>.corner
  expr: Constraints[26] = 3 + <<choices>>.screwhole_edge_margin
  expr: Constraints[29] = <<components>>.fan_w + <<choices>>.exit_w + <<choices>>.shroud_mb_space - <<choices>>.screwhole_edge_margin - 3
  expr: Constraints[39] = <<components>>.frame_h
  expr: Constraints[52] = <<choices>>.corner
  expr: Constraints[7] = <<choices>>.screwhole_edge_margin * 2
  expr: Constraints[8] = <<components>>.frame_h
  expr: Constraints[9] = <<components>>.frame_w
  sketch-geometry (21):
    g0: LineSegment StartX=365 StartY=0 StartZ=0 EndX=374 EndY=0 EndZ=0
    g1: LineSegment StartX=375 StartY=1 StartZ=0 EndX=375 EndY=228.5 EndZ=0
    g2: LineSegment StartX=374 StartY=229.5 StartZ=0 EndX=365 EndY=229.5 EndZ=0
    g3: LineSegment StartX=365 StartY=229.5 StartZ=0 EndX=365 EndY=0 EndZ=0
    g4: ArcOfCircle CenterX=374 CenterY=1 CenterZ=0 NormalX=0 NormalY=0 NormalZ=1 AngleXU=0 Radius=1 StartAngle=4.71239 EndAngle=6.28319
    g5: GeomPoint [constr] X=375 Y=0 Z=0
    g6: ArcOfCircle CenterX=374 CenterY=228.5 CenterZ=0 NormalX=0 NormalY=0 NormalZ=1 AngleXU=0 Radius=1 StartAngle=-3.6e-15 EndAngle=1.5708
    g7: GeomPoint [constr] X=375 Y=229.5 Z=0
    g8: LineSegment StartX=323 StartY=221.5 StartZ=0 EndX=323 EndY=228.5 EndZ=0
    g9: LineSegment StartX=323 StartY=228.5 StartZ=0 EndX=313 EndY=228.5 EndZ=0
    g10: LineSegment StartX=313 StartY=228.5 StartZ=0 EndX=313 EndY=221.5 EndZ=0
    g11: LineSegment StartX=0 StartY=228.5 StartZ=0 EndX=0 EndY=185.5 EndZ=0
    g12: LineSegment StartX=0 StartY=185.5 StartZ=0 EndX=10 EndY=185.5 EndZ=0
    g13: LineSegment StartX=10 StartY=185.5 StartZ=0 EndX=10 EndY=229.5 EndZ=0
    g14: LineSegment StartX=10 StartY=229.5 StartZ=0 EndX=1 EndY=229.5 EndZ=0
    g15: ArcOfCircle [constr] CenterX=318 CenterY=221.5 CenterZ=0 NormalX=0 NormalY=0 NormalZ=1 AngleXU=0 Radius=5 StartAngle=3.14159 EndAngle=4.71239
    g16: ArcOfCircle CenterX=318 CenterY=221.5 CenterZ=0 NormalX=0 NormalY=0 NormalZ=1 AngleXU=0 Radius=5 StartAngle=4.71239 EndAngle=6.28319
    g17: LineSegment StartX=313 StartY=221.5 StartZ=0 EndX=313 EndY=216.5 EndZ=0
    g18: LineSegment StartX=313 StartY=216.5 StartZ=0 EndX=318 EndY=216.5 EndZ=0
    g19: ArcOfCircle CenterX=1 CenterY=228.5 CenterZ=0 NormalX=0 NormalY=0 NormalZ=1 AngleXU=0 Radius=1 StartAngle=1.5708 EndAngle=3.14159
    g20: GeomPoint [constr] X=0 Y=229.5 Z=0
  constraints (54):
    c: Coincident(g2,g3)
    c: Coincident(g3,g0)
    c: Horizontal(g0)
    c: Horizontal(g2)
    c: Vertical(g1)
    c: Vertical(g3)
    c: PointOnObject(g0,g-1)
    c: DistanceX(g2,g7) = 10
    c: DistanceY(g5,g7) = 229.5
    c: DistanceX(g5) = 375
    c: PointOnObject(g5,g0)
    c: PointOnObject(g5,g1)
    c: Tangent(g0,g4) = -1.5708
    c: Tangent(g1,g4) = -1.5708
    c: PointOnObject(g7,g1)
    c: PointOnObject(g7,g2)
    c: Tangent(g1,g6) = -1.5708
    c: Tangent(g2,g6) = -1.5708
    c: Equal(g4,g6)
    c: Radius(g4) = 1
    c: Coincident(g8,g9)
    c: Coincident(g9,g10)
    c: Horizontal(g9)
    c: Vertical(g8)
    c: Vertical(g10)
    c: Distance(g8,g2) = 1
    c: Distance(g15,g2) = 8
    c: Tangent(g16,g8) = -1.5708
    c: Tangent(g15,g10) = -1.5708
    c: Distance(g15,g1) = 57
    c: Coincident(g11,g12)
    c: Coincident(g12,g13)
    c: Coincident(g13,g14)
    c: Vertical(g11)
    c: Vertical(g13)
    c: Horizontal(g12)
    c: Horizontal(g14)
    c: Distance(g20,g13) = 10
    c: Distance(g12,g20) = 44
    c: DistanceY(g20) = 229.5
    c: Coincident(g15,g16)
    c: Coincident(g15,g16)
    c: Diameter(g15) = 10
    c: Coincident(g10,g17)
    c: Vertical(g17)
    c: Coincident(g17,g18)
    c: Coincident(g18,g15)
    c: Horizontal(g18)
    c: PointOnObject(g20,g11)
    c: PointOnObject(g20,g14)
    c: Tangent(g11,g19) = -1.5708
    c: Tangent(g14,g19) = -1.5708
    c: Radius(g19) = 1
    c: PointOnObject(g11,g-2)
FEATURE [PartDesign::Pad] Pad024  label="3mm thick at the right end"
  BaseFeature = -> Pad020
  Direction = (0,0,1)
  Length = 3
  Length2 = 10
  Profile = -> Sketch045
  ReferenceAxis = -> Sketch045 [N_Axis]
  Refine = true
  Suppressed = false
  Type = 0
FEATURE [Sketcher::SketchObject] Sketch046
  ArcFitTolerance = 1e-06
  AttachmentSupport = -> [XY_Plane013]
  FullyConstrained = true
  MakeInternals = false
  MapMode = 5
  expr: Constraints[19] = <<components>>.fan_w + <<choices>>.exit_w + <<choices>>.shroud_mb_space - 2 * <<choices>>.screwhole_edge_margin - 3
  expr: Constraints[25] = <<choices>>.screwhole_edge_margin
  expr: Constraints[26] = <<choices>>.screwhole_edge_margin + 3
  expr: Constraints[2] = <<components>>.frame_h
  expr: Constraints[3] = <<components>>.frame_w - <<choices>>.screwhole_edge_margin
  expr: Constraints[6] = <<components>>.m3_hole
  expr: Constraints[7] = 3 + <<choices>>.screwhole_edge_margin
  expr: Constraints[8] = 3 + <<choices>>.screwhole_edge_margin
  sketch-geometry (10):
    g0: LineSegment [constr] StartX=370 StartY=0 StartZ=0 EndX=370 EndY=229.5 EndZ=0
    g1: Circle CenterX=370 CenterY=221.5 CenterZ=0 NormalX=0 NormalY=0 NormalZ=1 AngleXU=0 Radius=3
    g2: Circle CenterX=370 CenterY=8 CenterZ=0 NormalX=0 NormalY=0 NormalZ=1 AngleXU=0 Radius=1.75
    g3: Circle CenterX=370 CenterY=114.75 CenterZ=0 NormalX=0 NormalY=0 NormalZ=1 AngleXU=0 Radius=1.75
    g4: Circle CenterX=370 CenterY=213.5 CenterZ=0 NormalX=0 NormalY=0 NormalZ=1 AngleXU=0 Radius=1.75
    g5: Circle CenterX=318 CenterY=221.5 CenterZ=0 NormalX=0 NormalY=0 NormalZ=1 AngleXU=0 Radius=1.75
    g6: LineSegment [constr] StartX=318 StartY=221.5 StartZ=0 EndX=370 EndY=221.5 EndZ=0
    g7: LineSegment [constr] StartX=5 StartY=0 StartZ=0 EndX=5 EndY=221.5 EndZ=0
    g8: Circle CenterX=5 CenterY=8 CenterZ=0 NormalX=0 NormalY=0 NormalZ=1 AngleXU=0 Radius=1.75
    g9: Circle CenterX=5 CenterY=221.5 CenterZ=0 NormalX=0 NormalY=0 NormalZ=1 AngleXU=0 Radius=1.75
  constraints (29):
    c: PointOnObject(g0,g-1)
    c: Vertical(g0)
    c: DistanceY(g0,g0) = 229.5
    c: DistanceX(g0) = 370
    c: PointOnObject(g1,g0)
    c: PointOnObject(g2,g0)
    c: Diameter(g2) = 3.5
    c: DistanceY(g2) = 8
    c: Distance(g1,g0) = 8
    c: Symmetric(g0,g0,g3)
    c: Equal(g2,g3)
    c: PointOnObject(g4,g0)
    c: Equal(g3,g4)
    c: Distance(g4,g1) = 8
    c: Diameter(g1) = 6
    c: Equal(g5,g4)
    c: Coincident(g6,g5)
    c: Coincident(g6,g1)
    c: Horizontal(g6)
    c: DistanceX(g6,g6) = 52
    c: PointOnObject(g7,g-1)
    c: Vertical(g7)
    c: PointOnObject(g8,g7)
    c: Equal(g8,g9)
    c: Equal(g9,g4)
    c: DistanceX(g8) = 5
    c: DistanceY(g8) = 8
    c: Coincident(g7,g9)
    c: PointOnObject(g7,g6)
FEATURE [PartDesign::Pocket] Pocket012  label="right end screwholes"
  BaseFeature = -> Pad024
  Direction = (0,0,-1)
  Length = 5
  Length2 = 5
  Midplane = true
  Profile = -> Sketch046
  ReferenceAxis = -> Sketch046 [N_Axis]
  Refine = true
  Suppressed = false
  Type = 1
FEATURE [PartDesign::Chamfer] Chamfer001
  Angle = 45
  Base = -> Pocket012 [Edge662,Edge665,Edge667,Edge669,Edge670,Edge664]
  BaseFeature = -> Pocket012
  ChamferType = 0
  FlipDirection = false
  Refine = true
  Size = 1.75
  Size2 = 1
  SupportTransform = false
  Suppressed = false
  UseAllEdges = false
FEATURE [PartDesign::Fillet] Fillet001
  Base = -> Chamfer001 [Edge135]
  BaseFeature = -> Chamfer001
  Radius = 1
  Refine = true
  SupportTransform = false
  Suppressed = false
  UseAllEdges = false
  expr: Radius = <<choices>>.corner
FEATURE [Sketcher::SketchObject] Sketch048
  ArcFitTolerance = 1e-06
  AttachmentSupport = -> [XY_Plane013]
  FullyConstrained = false
  MakeInternals = false
  MapMode = 5
  expr: Constraints[18] = <<choices>>.leg_betweens
  expr: Constraints[19] = <<components>>.frame_w - <<components>>.fan_w - <<choices>>.exit_w - <<choices>>.shroud_mb_space - 170 - 14.5 + <<choices>>.leg_betweens
  expr: Constraints[20] = <<choices>>.leg_width + 2 * <<choices>>.leg_clearance
  expr: Constraints[34] = <<choices>>.leg_bracket_slot_end_dist_from_front + 10 + 1 + 5 + 1
  expr: Constraints[38] = <<components>>.m3_threadhole
  expr: Constraints[41] = <<components>>.m3_threadhole
  sketch-geometry (22):
    g0: LineSegment StartX=130.5 StartY=65.1827 StartZ=0 EndX=125.5 EndY=65.1827 EndZ=0
    g1: LineSegment StartX=125.5 StartY=65.1827 StartZ=0 EndX=125.5 EndY=82.1827 EndZ=0
    g2: LineSegment StartX=125.5 StartY=82.1827 StartZ=0 EndX=130.5 EndY=82.1827 EndZ=0
    g3: LineSegment StartX=130.5 StartY=82.1827 StartZ=0 EndX=130.5 EndY=65.1827 EndZ=0
    g4: LineSegment StartX=114.5 StartY=65.1827 StartZ=0 EndX=109.5 EndY=65.1827 EndZ=0
    g5: LineSegment StartX=114.5 StartY=187 StartZ=0 EndX=114.5 EndY=65.1827 EndZ=0
    g6: LineSegment StartX=109.5 StartY=65.1827 StartZ=0 EndX=104.5 EndY=65.1827 EndZ=0
    g7: LineSegment StartX=104.5 StartY=65.1827 StartZ=0 EndX=104.5 EndY=187 EndZ=0
    g8: LineSegment [constr] StartX=114.5 StartY=65.1827 StartZ=0 EndX=125.5 EndY=65.1827 EndZ=0
    g9: LineSegment [constr] StartX=104.5 StartY=65.1827 StartZ=0 EndX=93.5 EndY=65.1827 EndZ=0
    g10: LineSegment StartX=93.5 StartY=65.1827 StartZ=0 EndX=88.5 EndY=65.1827 EndZ=0
    g11: LineSegment StartX=88.5 StartY=65.1827 StartZ=0 EndX=88.5 EndY=82.1827 EndZ=0
    g12: LineSegment StartX=88.5 StartY=82.1827 StartZ=0 EndX=93.5 EndY=82.1827 EndZ=0
    g13: LineSegment StartX=93.5 StartY=82.1827 StartZ=0 EndX=93.5 EndY=65.1827 EndZ=0
    g14: LineSegment StartX=104.5 StartY=187 StartZ=0 EndX=114.5 EndY=187 EndZ=0
    g15: Circle CenterX=109.5 CenterY=182.5 CenterZ=0 NormalX=0 NormalY=0 NormalZ=1 AngleXU=0 Radius=1.25
    g16: LineSegment [constr] StartX=104.556 StartY=89.8173 StartZ=0 EndX=104.556 EndY=82 EndZ=0
    g17: LineSegment [constr] StartX=114.444 StartY=82.1827 StartZ=0 EndX=114.444 EndY=90.1827 EndZ=0
    g18: Circle CenterX=109.5 CenterY=86 CenterZ=0 NormalX=0 NormalY=0 NormalZ=1 AngleXU=0 Radius=1.25
    g19: LineSegment [constr] StartX=109.5 StartY=86 StartZ=0 EndX=114.5 EndY=86 EndZ=0
    g20: LineSegment [constr] StartX=109.5 StartY=86 StartZ=0 EndX=104.5 EndY=86 EndZ=0
    g21: LineSegment [constr] StartX=109.5 StartY=182.5 StartZ=0 EndX=109.5 EndY=187 EndZ=0
  constraints (61):
    c: Coincident(g0,g1)
    c: Coincident(g1,g2)
    c: Coincident(g2,g3)
    c: Coincident(g3,g0)
    c: Horizontal(g0)
    c: Horizontal(g2)
    c: Vertical(g1)
    c: Vertical(g3)
    c: Coincident(g5,g4)
    c: Horizontal(g4)
    c: Vertical(g5)
    c: Coincident(g6,g7)
    c: Horizontal(g6)
    c: Vertical(g7)
    c: Coincident(g8,g4)
    c: Coincident(g8,g0)
    c: Horizontal(g8)
    c: Equal(g0,g4)
    c: DistanceX(g0,g0) = 5
    c: DistanceX(g0) = 130.5
    c: DistanceX(g8,g8) = 11
    c: Equal(g6,g4)
    c: Coincident(g9,g6)
    c: Horizontal(g9)
    c: Coincident(g10,g11)
    c: Coincident(g11,g12)
    c: Coincident(g12,g13)
    c: Coincident(g13,g10)
    c: Horizontal(g10)
    c: Horizontal(g12)
    c: Vertical(g11)
    c: Vertical(g13)
    c: Coincident(g10,g9)
    c: Equal(g6,g10)
    c: DistanceY(g7) = 187
    c: DistanceY(g3,g3) = 17
    c: Equal(g13,g1)
    c: Horizontal(g14)
    c: Diameter(g15) = 2.5
    c: Vertical(g16)
    c: Vertical(g17)
    c: Diameter(g18) = 2.5
    c: Symmetric(g16,g17,g18)
    c: PointOnObject(g17,g2)
    c: DistanceY(g17,g17) = 8
    c: DistanceY(g18) = 86
    c: Coincident(g19,g18)
    c: PointOnObject(g19,g5)
    c: Horizontal(g19)
    c: Coincident(g20,g18)
    c: PointOnObject(g20,g7)
    c: Horizontal(g20)
    c: Equal(g19,g20)
    c: Coincident(g21,g15)
    c: Symmetric(g14,g14,g21)
    c: DistanceY(g21,g21) = 4.5
    c: Equal(g9,g8)
    c: Coincident(g6,g4)
    c: Coincident(g14,g7)
    c: Coincident(g14,g5)
    c: Vertical(g21)
FEATURE [Sketcher::SketchObject] Sketch049
  ArcFitTolerance = 1e-06
  AttachmentSupport = -> [XY_Plane013]
  FullyConstrained = false
  MakeInternals = false
  MapMode = 5
  expr: Constraints[29] = <<choices>>.leg_betweens
  expr: Constraints[30] = <<components>>.frame_w - <<components>>.fan_w - <<choices>>.exit_w - <<choices>>.shroud_mb_space - 170 - 14.5 + <<choices>>.leg_betweens
  expr: Constraints[31] = <<choices>>.leg_width + 2 * <<choices>>.leg_clearance
  expr: Constraints[45] = <<choices>>.leg_axis_dist_from_front
  sketch-geometry (21):
    g0: LineSegment [constr] StartX=130.5 StartY=68 StartZ=0 EndX=125.5 EndY=68 EndZ=0
    g1: LineSegment StartX=125.5 StartY=68 StartZ=0 EndX=125.5 EndY=194.23 EndZ=0
    g2: LineSegment [constr] StartX=125.5 StartY=194.23 StartZ=0 EndX=130.5 EndY=194.23 EndZ=0
    g3: LineSegment [constr] StartX=130.5 StartY=194.23 StartZ=0 EndX=130.5 EndY=68 EndZ=0
    g4: LineSegment [constr] StartX=114.5 StartY=68 StartZ=0 EndX=109.5 EndY=68 EndZ=0
    g5: LineSegment [constr] StartX=109.5 StartY=68 StartZ=0 EndX=109.5 EndY=194.23 EndZ=0
    g6: LineSegment [constr] StartX=109.5 StartY=194.23 StartZ=0 EndX=114.5 EndY=194.23 EndZ=0
    g7: LineSegment StartX=114.5 StartY=194.23 StartZ=0 EndX=114.5 EndY=68 EndZ=0
    g8: LineSegment [constr] StartX=109.5 StartY=68 StartZ=0 EndX=104.5 EndY=68 EndZ=0
    g9: LineSegment StartX=104.5 StartY=68 StartZ=0 EndX=104.5 EndY=194.23 EndZ=0
    g10: LineSegment [constr] StartX=104.5 StartY=194.23 StartZ=0 EndX=109.5 EndY=194.23 EndZ=0
    g11: LineSegment [constr] StartX=109.5 StartY=194.23 StartZ=0 EndX=109.5 EndY=68 EndZ=0
    g12: LineSegment StartX=114.5 StartY=68 StartZ=0 EndX=125.5 EndY=68 EndZ=0
    g13: LineSegment StartX=104.5 StartY=68 StartZ=0 EndX=93.5 EndY=68 EndZ=0
    g14: LineSegment [constr] StartX=93.5 StartY=68 StartZ=0 EndX=88.5 EndY=68 EndZ=0
    g15: LineSegment [constr] StartX=88.5 StartY=68 StartZ=0 EndX=88.5 EndY=194.23 EndZ=0
    g16: LineSegment [constr] StartX=88.5 StartY=194.23 StartZ=0 EndX=93.5 EndY=194.23 EndZ=0
    g17: LineSegment StartX=93.5 StartY=194.23 StartZ=0 EndX=93.5 EndY=68 EndZ=0
    g18: GeomPoint X=77.5 Y=75 Z=0
    g19: LineSegment StartX=93.5 StartY=194.23 StartZ=0 EndX=104.5 EndY=194.23 EndZ=0
    g20: LineSegment StartX=114.5 StartY=194.23 StartZ=0 EndX=125.5 EndY=194.23 EndZ=0
  constraints (56):
    c: Coincident(g0,g1)
    c: Coincident(g1,g2)
    c: Coincident(g2,g3)
    c: Coincident(g3,g0)
    c: Horizontal(g0)
    c: Horizontal(g2)
    c: Vertical(g1)
    c: Vertical(g3)
    c: Coincident(g4,g5)
    c: Coincident(g5,g6)
    c: Coincident(g6,g7)
    c: Coincident(g7,g4)
    c: Horizontal(g4)
    c: Horizontal(g6)
    c: Vertical(g5)
    c: Vertical(g7)
    c: Coincident(g8,g9)
    c: Coincident(g9,g10)
    c: Coincident(g10,g11)
    c: Coincident(g11,g8)
    c: Horizontal(g8)
    c: Horizontal(g10)
    c: Vertical(g9)
    c: Vertical(g11)
    c: Coincident(g12,g4)
    c: Coincident(g12,g0)
    c: Horizontal(g12)
    c: Equal(g0,g4)
    c: Equal(g11,g5)
    c: DistanceX(g0,g0) = 5
    c: DistanceX(g0) = 130.5
    c: DistanceX(g12,g12) = 11
    c: Equal(g8,g4)
    c: Coincident(g13,g8)
    c: Horizontal(g13)
    c: Coincident(g14,g15)
    c: Coincident(g15,g16)
    c: Coincident(g16,g17)
    c: Coincident(g17,g14)
    c: Horizontal(g14)
    c: Horizontal(g16)
    c: Vertical(g15)
    c: Vertical(g17)
    c: Coincident(g14,g13)
    c: Equal(g8,g14)
    c: DistanceY(g18) = 75
    c: Equal(g17,g1)
    c: Distance(g18,g13) = 7
    c: Coincident(g19,g16)
    c: Coincident(g19,g9)
    c: Coincident(g20,g6)
    c: Coincident(g20,g1)
    c: Horizontal(g19)
    c: DistanceY(g16) = 194.23
    c: Equal(g13,g12)
    c: Coincident(g8,g4)
FEATURE [PartDesign::Plane] DatumPlane007
  AttachmentOffset = pos=(0,0,109.5) rot=(0,0,1;0rad)
  AttachmentSupport = -> [YZ_Plane013]
  Length = 277.061
  MapMode = 5
  Placement = pos=(109.5,0,0) rot=(0.57735,0.57735,0.57735;2.0944rad)
  ResizeMode = 0
  Width = 72.561
FEATURE [Sketcher::SketchObject] Sketch050
  ArcFitTolerance = 1e-06
  AttachmentSupport = -> [DatumPlane007]
  FullyConstrained = false
  MakeInternals = false
  MapMode = 5
  Placement = pos=(109.5,0,0) rot=(0.57735,0.57735,0.57735;2.0944rad)
  expr: Constraints[33] = <<choices>>.leg_axle_hole_dia
  expr: Constraints[77] = <<choices>>.leg_axle_hole_dia / 2
  expr: Constraints[78] = <<choices>>.leg_axis_dist_from_front
  expr: Constraints[8] = <<choices>>.leg_bracket_slot_end_dist_from_front - <<choices>>.leg_bracket_slot_start_dist_from_front - 1
  expr: Constraints[9] = <<choices>>.leg_bracket_slot_end_dist_from_front + 0.5 * <<choices>>.leg_axle_hole_dia + 1
  sketch-geometry (29):
    g0: LineSegment StartX=173.6 StartY=7.5 StartZ=0 EndX=173.6 EndY=12.5 EndZ=0
    g1: LineSegment [constr] StartX=173.6 StartY=12.5 StartZ=0 EndX=112.764 EndY=12.5 EndZ=0
    g2: LineSegment StartX=119.6 StartY=12.5 StartZ=0 EndX=119.6 EndY=7.5 EndZ=0
    g3: LineSegment [constr] StartX=119.6 StartY=7.5 StartZ=0 EndX=173.6 EndY=7.5 EndZ=0
    g4: LineSegment StartX=173.6 StartY=12.5 StartZ=0 EndX=168.4 EndY=12.5 EndZ=0
    g5: LineSegment StartX=168.4 StartY=12.5 StartZ=0 EndX=164.6 EndY=7.5 EndZ=0
    g6: LineSegment StartX=164.6 StartY=7.5 StartZ=0 EndX=164.6 EndY=12.5 EndZ=0
    g7: LineSegment StartX=164.6 StartY=12.5 StartZ=0 EndX=159.4 EndY=12.5 EndZ=0
    g8: LineSegment StartX=159.4 StartY=12.5 StartZ=0 EndX=155.6 EndY=7.5 EndZ=0
    g9: LineSegment StartX=155.6 StartY=7.5 StartZ=0 EndX=155.6 EndY=12.5 EndZ=0
    g10: LineSegment StartX=155.6 StartY=12.5 StartZ=0 EndX=150.4 EndY=12.5 EndZ=0
    g11: LineSegment StartX=150.4 StartY=12.5 StartZ=0 EndX=146.6 EndY=7.5 EndZ=0
    g12: LineSegment StartX=146.6 StartY=7.5 StartZ=0 EndX=146.6 EndY=12.5 EndZ=0
    g13: LineSegment StartX=146.6 StartY=12.5 StartZ=0 EndX=141.4 EndY=12.5 EndZ=0
    g14: LineSegment StartX=141.4 StartY=12.5 StartZ=0 EndX=137.6 EndY=7.5 EndZ=0
    g15: LineSegment StartX=137.6 StartY=7.5 StartZ=0 EndX=137.6 EndY=12.5 EndZ=0
    g16: LineSegment StartX=137.6 StartY=12.5 StartZ=0 EndX=132.4 EndY=12.5 EndZ=0
    g17: LineSegment StartX=132.4 StartY=12.5 StartZ=0 EndX=128.6 EndY=7.5 EndZ=0
    g18: LineSegment StartX=128.6 StartY=7.5 StartZ=0 EndX=128.6 EndY=12.5 EndZ=0
    g19: LineSegment StartX=128.6 StartY=12.5 StartZ=0 EndX=123.4 EndY=12.5 EndZ=0
    g20: LineSegment StartX=123.4 StartY=12.5 StartZ=0 EndX=119.6 EndY=7.5 EndZ=0
    g21: LineSegment StartX=119.6 StartY=12.5 StartZ=0 EndX=107 EndY=12.5 EndZ=0
    g22: LineSegment StartX=107 StartY=12.5 StartZ=0 EndX=107 EndY=-4.82574 EndZ=0
    g23: LineSegment StartX=107 StartY=-4.82574 StartZ=0 EndX=173.6 EndY=-4.82574 EndZ=0
    g24: LineSegment StartX=173.6 StartY=-4.82574 StartZ=0 EndX=173.6 EndY=7.5 EndZ=0
    g25: ArcOfCircle CenterX=75 CenterY=5.87086 CenterZ=0 NormalX=0 NormalY=0 NormalZ=1 AngleXU=0 Radius=2.6 StartAngle=2e-16 EndAngle=3.14159
    g26: ArcOfCircle CenterX=75 CenterY=-13.8999 CenterZ=0 NormalX=0 NormalY=0 NormalZ=1 AngleXU=0 Radius=2.6 StartAngle=3.14159 EndAngle=6.28319
    g27: LineSegment StartX=77.6 StartY=5.87086 StartZ=0 EndX=77.6 EndY=-13.8999 EndZ=0
    g28: LineSegment StartX=72.4 StartY=5.87086 StartZ=0 EndX=72.4 EndY=-13.8999 EndZ=0
  constraints (79):
    c: Vertical(g0)
    c: Coincident(g1,g0)
    c: Horizontal(g1)
    c: PointOnObject(g2,g1)
    c: Vertical(g2)
    c: Coincident(g3,g2)
    c: Coincident(g3,g0)
    c: Horizontal(g3)
    c: DistanceX(g2,g0) = 54
    c: DistanceX(g0) = 173.6
    c: Coincident(g0,g4)
    c: PointOnObject(g4,g1)
    c: Coincident(g4,g5)
    c: PointOnObject(g5,g3)
    c: Coincident(g5,g6)
    c: PointOnObject(g6,g1)
    c: Vertical(g6)
    c: Coincident(g6,g7)
    c: PointOnObject(g7,g1)
    c: Coincident(g7,g8)
    c: PointOnObject(g8,g3)
    c: Coincident(g8,g9)
    c: PointOnObject(g9,g1)
    c: Vertical(g9)
    c: Coincident(g9,g10)
    c: PointOnObject(g10,g1)
    c: Coincident(g10,g11)
    c: PointOnObject(g11,g3)
    c: Coincident(g11,g12)
    c: Coincident(g12,g13)
    c: PointOnObject(g13,g1)
    c: Coincident(g13,g14)
    c: Vertical(g12)
    c: DistanceX(g4,g4) = 5.2
    c: Equal(g4,g7)
    c: Equal(g7,g10)
    c: Equal(g10,g13)
    c: Equal(g5,g8)
    c: Equal(g8,g11)
    c: Equal(g11,g14)
    c: Coincident(g14,g15)
    c: PointOnObject(g15,g1)
    c: Vertical(g15)
    c: Coincident(g15,g16)
    c: PointOnObject(g16,g1)
    c: Coincident(g16,g17)
    c: Coincident(g17,g18)
    c: PointOnObject(g18,g1)
    c: Vertical(g18)
    c: Coincident(g18,g19)
    c: PointOnObject(g19,g1)
    c: Coincident(g19,g20)
    c: Coincident(g20,g2)
    c: Coincident(g2,g21)
    c: PointOnObject(g21,g1)
    c: Coincident(g21,g22)
    c: Vertical(g22)
    c: Coincident(g22,g23)
    c: Horizontal(g23)
    c: Coincident(g23,g24)
    c: Coincident(g24,g0)
    c: Vertical(g24)
    c: Equal(g19,g16)
    c: Equal(g16,g13)
    c: Equal(g20,g17)
    c: Equal(g17,g14)
    c: PointOnObject(g14,g3)
    c: PointOnObject(g17,g3)
    c: DistanceY(g5) = 7.5
    c: Horizontal(g13)
    c: DistanceY(g0) = 12.5
    c: Tangent(g25,g27) = 1.5708
    c: Tangent(g25,g28) = -1.5708
    c: Tangent(g26,g27) = 1.5708
    c: Tangent(g26,g28) = -1.5708
    c: Equal(g25,g26)
    c: Vertical(g27)
    c: Radius(g25) = 2.6
    c: DistanceX(g25) = 75
FEATURE [Sketcher::SketchObject] Sketch051
  ArcFitTolerance = 1e-06
  AttachmentSupport = -> [DatumPlane007]
  FullyConstrained = true
  MakeInternals = false
  MapMode = 5
  Placement = pos=(109.5,0,0) rot=(0.57735,0.57735,0.57735;2.0944rad)
  expr: Constraints[0] = <<choices>>.leg_axle_hole_dia
  expr: Constraints[2] = <<choices>>.leg_axis_dist_from_front
  sketch-geometry (1):
    g0: Circle CenterX=75 CenterY=5 CenterZ=0 NormalX=0 NormalY=0 NormalZ=1 AngleXU=0 Radius=2.6
  constraints (3):
    c: Diameter(g0) = 5.2
    c: DistanceY(g0) = 5
    c: DistanceX(g0) = 75
FEATURE [PartDesign::Plane] DatumPlane008
  AttachmentOffset = pos=(0,0,26) rot=(0,0,1;0rad)
  AttachmentSupport = -> [DatumPlane007]
  Length = 277.061
  MapMode = 5
  Placement = pos=(135.5,0,0) rot=(0.57735,0.57735,0.57735;2.0944rad)
  ResizeMode = 0
  Width = 72.561
FEATURE [Sketcher::SketchObject] Sketch052
  ArcFitTolerance = 1e-06
  AttachmentSupport = -> [DatumPlane008]
  FullyConstrained = false
  MakeInternals = false
  MapMode = 5
  Placement = pos=(135.5,0,0) rot=(0.57735,0.57735,0.57735;2.0944rad)
  expr: Constraints[6] = <<choices>>.leg_axle_hole_dia / 2
  expr: Constraints[8] = <<choices>>.leg_axis_dist_from_front
  sketch-geometry (4):
    g0: ArcOfCircle CenterX=75 CenterY=5 CenterZ=0 NormalX=0 NormalY=0 NormalZ=1 AngleXU=0 Radius=2.6 StartAngle=3.14159 EndAngle=6.28319
    g1: ArcOfCircle CenterX=75 CenterY=26.5817 CenterZ=0 NormalX=0 NormalY=0 NormalZ=1 AngleXU=0 Radius=2.6 StartAngle=0 EndAngle=3.14159
    g2: LineSegment StartX=72.4 StartY=5 StartZ=0 EndX=72.4 EndY=26.5817 EndZ=0
    g3: LineSegment StartX=77.6 StartY=5 StartZ=0 EndX=77.6 EndY=26.5817 EndZ=0
  constraints (9):
    c: Tangent(g0,g2) = 1.5708
    c: Tangent(g0,g3) = -1.5708
    c: Tangent(g1,g2) = 1.5708
    c: Tangent(g1,g3) = -1.5708
    c: Equal(g0,g1)
    c: Vertical(g2)
    c: Radius(g1) = 2.6
    c: DistanceY(g0) = 5
    c: DistanceX(g0) = 75
FEATURE [PartDesign::Pocket] Pocket022
  BaseFeature = -> Fillet001
  Direction = (0,0,-1)
  Length = 17.6
  Length2 = 5
  Profile = -> Sketch053
  ReferenceAxis = -> Sketch053 [N_Axis]
  Refine = true
  Suppressed = false
  Type = 0
  expr: Length = <<choices>>.base_max_thickness - 2.4
FEATURE [PartDesign::Pocket] Pocket023
  BaseFeature = -> Pocket022
  Direction = (0,0,-1)
  Length = 15
  Length2 = 5
  Profile = -> Sketch049 [Edge3,Edge1,Edge5,Edge7,Edge6,Edge4,Edge2,Edge8]
  ReferenceAxis = -> Sketch049 [N_Axis]
  Refine = true
  Reversed = true
  Suppressed = false
  Type = 0
FEATURE [PartDesign::Pad] Pad025
  BaseFeature = -> Pocket023
  Direction = (0,0,1)
  Length = 15
  Length2 = 10
  Profile = -> Sketch048
  ReferenceAxis = -> Sketch048 [N_Axis]
  Refine = true
  Suppressed = false
  Type = 0
FEATURE [Sketcher::SketchObject] Sketch054
  ArcFitTolerance = 1e-06
  AttachmentSupport = -> [XY_Plane013]
  FullyConstrained = false
  MakeInternals = false
  MapMode = 5
  sketch-geometry (4):
    g0: LineSegment StartX=95.1754 StartY=192.602 StartZ=0 EndX=95.1754 EndY=67 EndZ=0
    g1: LineSegment StartX=95.1754 StartY=67 StartZ=0 EndX=114.794 EndY=67 EndZ=0
    g2: LineSegment StartX=114.794 StartY=67 StartZ=0 EndX=114.794 EndY=192.602 EndZ=0
    g3: LineSegment StartX=114.794 StartY=192.602 StartZ=0 EndX=95.1754 EndY=192.602 EndZ=0
  constraints (9):
    c: Coincident(g0,g1)
    c: Coincident(g1,g2)
    c: Coincident(g2,g3)
    c: Coincident(g3,g0)
    c: Vertical(g0)
    c: Vertical(g2)
    c: Horizontal(g1)
    c: Horizontal(g3)
    c: DistanceY(g0) = 67
FEATURE [PartDesign::Pad] Pad038
  BaseFeature = -> Pad025
  Direction = (0,0,1)
  Length = 20
  Length2 = 10
  Profile = -> Sketch078
  ReferenceAxis = -> Sketch078 [N_Axis]
  Refine = true
  Suppressed = false
  Type = 0
  expr: Length = <<choices>>.base_max_thickness
FEATURE [PartDesign::Pocket] Pocket019
  BaseFeature = -> Pad038
  Direction = (-1,0,0)
  Length = 10
  Length2 = 5
  Midplane = true
  Profile = -> Sketch050
  ReferenceAxis = -> Sketch050 [N_Axis]
  Refine = true
  Suppressed = false
  Type = 0
FEATURE [PartDesign::Pocket] Pocket020
  BaseFeature = -> Pocket019
  Direction = (-1,0,0)
  Length = 62
  Length2 = 5
  Midplane = true
  Profile = -> Sketch051
  ReferenceAxis = -> Sketch051 [N_Axis]
  Refine = true
  Suppressed = false
  Type = 0
FEATURE [PartDesign::Pocket] Pocket021
  BaseFeature = -> Pocket020
  Direction = (-1,0,0)
  Length = 30
  Length2 = 5
  Midplane = true
  Profile = -> Sketch052
  ReferenceAxis = -> Sketch052 [N_Axis]
  Refine = true
  Suppressed = false
  Type = 0
FEATURE [PartDesign::Mirrored] Mirrored001
  BaseFeature = -> Pocket021
  MirrorPlane = -> DatumPlane007
  Originals = -> [Pocket021]
  Refine = true
  Suppressed = false
  TransformMode = 0
FEATURE [PartDesign::Body] Body006
  AllowCompound = false
  Group = -> [Sketch014,Pad011,Sketch016,Pad013,Sketch017,Pad014,Sketch018,Pocket004,Sketch019,Pocket005,Sketch020,Pocket006,Pocket007,Sketch021,LinearPattern,DatumPlane001,Sketch035,Pad020,Sketch045,Pad024,Sketch046,Pocket012,Chamfer001,Fillet001,Pocket022,Pocket023,Sketch054,Sketch048,Pad025,Sketch049,DatumPlane007,Sketch050,Pad038,Pocket019,Sketch051,Pocket020,DatumPlane008,Sketch052,Pocket021,Mirrored001,+8 more]
  Origin = -> Origin013
  Tip = -> Pad045
COMPONENT P1 — recipe-attached ("EXIT_DUCT001", modeled in this document).
Construction recipe (the document's own serialized feature program — sketch geometry with constraints, then the solid features built on it; lengths are millimeters unless a unit is written):

FEATURE [Sketcher::SketchObject] Sketch015
  ArcFitTolerance = 1e-06
  AttachmentSupport = -> [XY_Plane015]
  FullyConstrained = true
  MakeInternals = false
  MapMode = 5
  expr: Constraints[18] = <<choices>>.corner
  expr: Constraints[7] = <<choices>>.exit_w
  expr: Constraints[8] = <<components>>.frame_h
  sketch-geometry (8):
    g0: LineSegment StartX=0 StartY=0 StartZ=0 EndX=18 EndY=0 EndZ=0
    g1: LineSegment StartX=19 StartY=1 StartZ=0 EndX=19 EndY=228.5 EndZ=0
    g2: LineSegment StartX=18 StartY=229.5 StartZ=0 EndX=0 EndY=229.5 EndZ=0
    g3: LineSegment StartX=0 StartY=229.5 StartZ=0 EndX=0 EndY=0 EndZ=0
    g4: ArcOfCircle CenterX=18 CenterY=228.5 CenterZ=0 NormalX=0 NormalY=0 NormalZ=1 AngleXU=0 Radius=1 StartAngle=9.6e-15 EndAngle=1.5708
    g5: GeomPoint [constr] X=19 Y=229.5 Z=0
    g6: ArcOfCircle CenterX=18 CenterY=1 CenterZ=0 NormalX=0 NormalY=0 NormalZ=1 AngleXU=0 Radius=1 StartAngle=4.71239 EndAngle=6.28319
    g7: GeomPoint [constr] X=19 Y=0 Z=0
  constraints (19):
    c: Coincident(g2,g3)
    c: Coincident(g3,g0)
    c: Horizontal(g0)
    c: Horizontal(g2)
    c: Vertical(g1)
    c: Vertical(g3)
    c: Coincident(g0,g-1)
    c: DistanceX(g2,g5) = 19
    c: DistanceY(g7,g5) = 229.5
    c: PointOnObject(g5,g1)
    c: PointOnObject(g5,g2)
    c: Tangent(g1,g4) = -1.5708
    c: Tangent(g2,g4) = -1.5708
    c: PointOnObject(g7,g0)
    c: PointOnObject(g7,g1)
    c: Tangent(g0,g6) = -1.5708
    c: Tangent(g1,g6) = -1.5708
    c: Equal(g4,g6)
    c: Radius(g4) = 1
FEATURE [PartDesign::Pad] Pad012
  Direction = (0,0,1)
  Length = 55
  Length2 = 10
  Profile = -> Sketch015
  ReferenceAxis = -> Sketch015 [N_Axis]
  Refine = true
  Suppressed = false
  Type = 0
  expr: Length = <<choices>>.exit_height
FEATURE [Sketcher::SketchObject] Sketch022
  ArcFitTolerance = 1e-06
  AttachmentSupport = -> [YZ_Plane015]
  FullyConstrained = true
  MakeInternals = false
  MapMode = 5
  Placement = pos=(0,0,0) rot=(0.57735,0.57735,0.57735;2.0944rad)
  expr: Constraints[21] = <<components>>.frame_h
  expr: Constraints[9] = <<choices>>.base_max_thickness - 3
  sketch-geometry (8):
    g0: LineSegment StartX=0 StartY=0 StartZ=0 EndX=3 EndY=0 EndZ=0
    g1: LineSegment StartX=3 StartY=0 StartZ=0 EndX=3 EndY=17 EndZ=0
    g2: LineSegment StartX=3 StartY=17 StartZ=0 EndX=0 EndY=17 EndZ=0
    g3: LineSegment StartX=0 StartY=17 StartZ=0 EndX=0 EndY=0 EndZ=0
    g4: LineSegment StartX=226.5 StartY=0 StartZ=0 EndX=229.5 EndY=0 EndZ=0
    g5: LineSegment StartX=229.5 StartY=0 StartZ=0 EndX=229.5 EndY=17 EndZ=0
    g6: LineSegment StartX=229.5 StartY=17 StartZ=0 EndX=226.5 EndY=17 EndZ=0
    g7: LineSegment StartX=226.5 StartY=17 StartZ=0 EndX=226.5 EndY=0 EndZ=0
  constraints (23):
    c: Coincident(g0,g1)
    c: Coincident(g1,g2)
    c: Coincident(g2,g3)
    c: Coincident(g3,g0)
    c: Horizontal(g0)
    c: Horizontal(g2)
    c: Vertical(g1)
    c: Vertical(g3)
    c: Distance(g1,g3) = 3
    c: Distance(g0,g2) = 17
    c: Coincident(g0,g-1)
    c: Coincident(g4,g5)
    c: Coincident(g5,g6)
    c: Coincident(g6,g7)
    c: Coincident(g7,g4)
    c: Horizontal(g4)
    c: Horizontal(g6)
    c: Vertical(g5)
    c: Vertical(g7)
    c: Distance(g5,g7) = 3
    c: PointOnObject(g4,g-1)
    c: DistanceX(g4) = 229.5
    c: PointOnObject(g6,g2)
FEATURE [PartDesign::Plane] DatumPlane002
  AttachmentOffset = pos=(0,0,19) rot=(0,0,1;0rad)
  AttachmentSupport = -> [YZ_Plane015]
  Length = 283.038
  MapMode = 5
  Placement = pos=(19,0,0) rot=(0.57735,0.57735,0.57735;2.0944rad)
  ResizeMode = 0
  Width = 108.538
  expr: .AttachmentOffset.Base.z = <<choices>>.exit_w
FEATURE [Sketcher::SketchObject] Sketch023
  ArcFitTolerance = 1e-06
  AttachmentSupport = -> [YZ_Plane015]
  FullyConstrained = true
  MakeInternals = false
  MapMode = 5
  Placement = pos=(0,0,0) rot=(0.57735,0.57735,0.57735;2.0944rad)
  expr: Constraints[104] = <<components>>.fan_spacing
  expr: Constraints[10] = <<choices>>.exit_height
  expr: Constraints[136] = <<components>>.m3_hole
  expr: Constraints[137] = <<choices>>.fan_gap
  expr: Constraints[138] = <<choices>>.fan_gap
  expr: Constraints[139] = <<choices>>.fan_gap
  expr: Constraints[21] = <<choices>>.exit_height
  expr: Constraints[32] = <<choices>>.exit_height
  expr: Constraints[43] = <<choices>>.exit_height
  expr: Constraints[56] = <<choices>>.exit_fan_dia
  sketch-geometry (60):
    g0: LineSegment [constr] StartX=4 StartY=0 StartZ=0 EndX=54 EndY=0 EndZ=0
    g1: LineSegment [constr] StartX=54 StartY=0 StartZ=0 EndX=54 EndY=55 EndZ=0
    g2: LineSegment [constr] StartX=54 StartY=55 StartZ=0 EndX=4 EndY=55 EndZ=0
    g3: LineSegment [constr] StartX=4 StartY=55 StartZ=0 EndX=4 EndY=0 EndZ=0
    g4: GeomPoint [constr] X=29 Y=27.5 Z=0
    g5: LineSegment [constr] StartX=56 StartY=0 StartZ=0 EndX=106 EndY=0 EndZ=0
    g6: LineSegment [constr] StartX=106 StartY=0 StartZ=0 EndX=106 EndY=55 EndZ=0
    g7: LineSegment [constr] StartX=106 StartY=55 StartZ=0 EndX=56 EndY=55 EndZ=0
    g8: LineSegment [constr] StartX=56 StartY=55 StartZ=0 EndX=56 EndY=0 EndZ=0
    g9: GeomPoint [constr] X=81 Y=27.5 Z=0
    g10: LineSegment [constr] StartX=108 StartY=0 StartZ=0 EndX=158 EndY=0 EndZ=0
    g11: LineSegment [constr] StartX=158 StartY=0 StartZ=0 EndX=158 EndY=55 EndZ=0
    g12: LineSegment [constr] StartX=158 StartY=55 StartZ=0 EndX=108 EndY=55 EndZ=0
    g13: LineSegment [constr] StartX=108 StartY=55 StartZ=0 EndX=108 EndY=0 EndZ=0
    g14: GeomPoint [constr] X=133 Y=27.5 Z=0
    g15: LineSegment [constr] StartX=160 StartY=0 StartZ=0 EndX=210 EndY=0 EndZ=0
    g16: LineSegment [constr] StartX=210 StartY=0 StartZ=0 EndX=210 EndY=55 EndZ=0
    g17: LineSegment [constr] StartX=210 StartY=55 StartZ=0 EndX=160 EndY=55 EndZ=0
    g18: LineSegment [constr] StartX=160 StartY=55 StartZ=0 EndX=160 EndY=0 EndZ=0
    g19: GeomPoint [constr] X=185 Y=27.5 Z=0
    g20: Circle CenterX=29 CenterY=27.5 CenterZ=0 NormalX=0 NormalY=0 NormalZ=1 AngleXU=0 Radius=24.5
    g21: Circle CenterX=81 CenterY=27.5 CenterZ=0 NormalX=0 NormalY=0 NormalZ=1 AngleXU=0 Radius=24.5
    g22: Circle CenterX=133 CenterY=27.5 CenterZ=0 NormalX=0 NormalY=0 NormalZ=1 AngleXU=0 Radius=24.5
    g23: Circle CenterX=185 CenterY=27.5 CenterZ=0 NormalX=0 NormalY=0 NormalZ=1 AngleXU=0 Radius=24.5
    g24: LineSegment [constr] StartX=49 StartY=7.5 StartZ=0 EndX=49 EndY=47.5 EndZ=0
    g25: LineSegment [constr] StartX=49 StartY=47.5 StartZ=0 EndX=9 EndY=47.5 EndZ=0
    g26: LineSegment [constr] StartX=9 StartY=47.5 StartZ=0 EndX=9 EndY=7.5 EndZ=0
    g27: LineSegment [constr] StartX=9 StartY=7.5 StartZ=0 EndX=49 EndY=7.5 EndZ=0
    g28: GeomPoint [constr] X=29 Y=27.5 Z=0
    g29: LineSegment [constr] StartX=101 StartY=7.5 StartZ=0 EndX=101 EndY=47.5 EndZ=0
    g30: LineSegment [constr] StartX=101 StartY=47.5 StartZ=0 EndX=61 EndY=47.5 EndZ=0
    g31: LineSegment [constr] StartX=61 StartY=47.5 StartZ=0 EndX=61 EndY=7.5 EndZ=0
    g32: LineSegment [constr] StartX=61 StartY=7.5 StartZ=0 EndX=101 EndY=7.5 EndZ=0
    g33: GeomPoint [constr] X=81 Y=27.5 Z=0
    g34: LineSegment [constr] StartX=153 StartY=7.5 StartZ=0 EndX=153 EndY=47.5 EndZ=0
    g35: LineSegment [constr] StartX=153 StartY=47.5 StartZ=0 EndX=113 EndY=47.5 EndZ=0
    g36: LineSegment [constr] StartX=113 StartY=47.5 StartZ=0 EndX=113 EndY=7.5 EndZ=0
    g37: LineSegment [constr] StartX=113 StartY=7.5 StartZ=0 EndX=153 EndY=7.5 EndZ=0
    g38: GeomPoint [constr] X=133 Y=27.5 Z=0
    g39: LineSegment [constr] StartX=205 StartY=7.5 StartZ=0 EndX=205 EndY=47.5 EndZ=0
    g40: LineSegment [constr] StartX=205 StartY=47.5 StartZ=0 EndX=165 EndY=47.5 EndZ=0
    g41: LineSegment [constr] StartX=165 StartY=47.5 StartZ=0 EndX=165 EndY=7.5 EndZ=0
    g42: LineSegment [constr] StartX=165 StartY=7.5 StartZ=0 EndX=205 EndY=7.5 EndZ=0
    g43: GeomPoint [constr] X=185 Y=27.5 Z=0
    g44: Circle [constr] CenterX=9 CenterY=47.5 CenterZ=0 NormalX=0 NormalY=0 NormalZ=1 AngleXU=0 Radius=1.75
    g45: Circle [constr] CenterX=49 CenterY=47.5 CenterZ=0 NormalX=0 NormalY=0 NormalZ=1 AngleXU=0 Radius=1.75
    g46: Circle [constr] CenterX=61 CenterY=47.5 CenterZ=0 NormalX=0 NormalY=0 NormalZ=1 AngleXU=0 Radius=1.75
    g47: Circle [constr] CenterX=9 CenterY=7.5 CenterZ=0 NormalX=0 NormalY=0 NormalZ=1 AngleXU=0 Radius=1.75
    g48: Circle [constr] CenterX=49 CenterY=7.5 CenterZ=0 NormalX=0 NormalY=0 NormalZ=1 AngleXU=0 Radius=1.75
    g49: Circle [constr] CenterX=61 CenterY=7.5 CenterZ=0 NormalX=0 NormalY=0 NormalZ=1 AngleXU=0 Radius=1.75
    g50: Circle [constr] CenterX=101 CenterY=7.5 CenterZ=0 NormalX=0 NormalY=0 NormalZ=1 AngleXU=0 Radius=1.75
    g51: Circle [constr] CenterX=113 CenterY=7.5 CenterZ=0 NormalX=0 NormalY=0 NormalZ=1 AngleXU=0 Radius=1.75
    g52: Circle [constr] CenterX=153 CenterY=7.5 CenterZ=0 NormalX=0 NormalY=0 NormalZ=1 AngleXU=0 Radius=1.75
    g53: Circle [constr] CenterX=165 CenterY=7.5 CenterZ=0 NormalX=0 NormalY=0 NormalZ=1 AngleXU=0 Radius=1.75
    g54: Circle [constr] CenterX=205 CenterY=7.5 CenterZ=0 NormalX=0 NormalY=0 NormalZ=1 AngleXU=0 Radius=1.75
    g55: Circle [constr] CenterX=205 CenterY=47.5 CenterZ=0 NormalX=0 NormalY=0 NormalZ=1 AngleXU=0 Radius=1.75
    g56: Circle [constr] CenterX=165 CenterY=47.5 CenterZ=0 NormalX=0 NormalY=0 NormalZ=1 AngleXU=0 Radius=1.75
    g57: Circle [constr] CenterX=153 CenterY=47.5 CenterZ=0 NormalX=0 NormalY=0 NormalZ=1 AngleXU=0 Radius=1.75
    g58: Circle [constr] CenterX=113 CenterY=47.5 CenterZ=0 NormalX=0 NormalY=0 NormalZ=1 AngleXU=0 Radius=1.75
    g59: Circle [constr] CenterX=101 CenterY=47.5 CenterZ=0 NormalX=0 NormalY=0 NormalZ=1 AngleXU=0 Radius=1.75
  constraints (140):
    c: Coincident(g0,g1)
    c: Coincident(g1,g2)
    c: Coincident(g2,g3)
    c: Coincident(g3,g0)
    c: Horizontal(g0)
    c: Horizontal(g2)
    c: Vertical(g1)
    c: Vertical(g3)
    c: Symmetric(g2,g0,g4)
    c: Distance(g1,g3) = 50
    c: Distance(g0,g2) = 55
    c: Coincident(g5,g6)
    c: Coincident(g6,g7)
    c: Coincident(g7,g8)
    c: Coincident(g8,g5)
    c: Horizontal(g5)
    c: Horizontal(g7)
    c: Vertical(g6)
    c: Vertical(g8)
    c: Symmetric(g7,g5,g9)
    c: Distance(g6,g8) = 50
    c: Distance(g5,g7) = 55
    c: Coincident(g10,g11)
    c: Coincident(g11,g12)
    c: Coincident(g12,g13)
    c: Coincident(g13,g10)
    c: Horizontal(g10)
    c: Horizontal(g12)
    c: Vertical(g11)
    c: Vertical(g13)
    c: Symmetric(g12,g10,g14)
    c: Distance(g11,g13) = 50
    c: Distance(g10,g12) = 55
    c: Coincident(g15,g16)
    c: Coincident(g16,g17)
    c: Coincident(g17,g18)
    c: Coincident(g18,g15)
    c: Horizontal(g15)
    c: Horizontal(g17)
    c: Vertical(g16)
    c: Vertical(g18)
    c: Symmetric(g17,g15,g19)
    c: Distance(g16,g18) = 50
    c: Distance(g15,g17) = 55
    c: PointOnObject(g0,g-1)
    c: PointOnObject(g5,g-1)
    c: PointOnObject(g10,g-1)
    c: PointOnObject(g15,g-1)
    c: DistanceX(g0) = 4
    c: Coincident(g20,g4)
    c: Coincident(g21,g9)
    c: Coincident(g22,g14)
    c: Coincident(g23,g19)
    c: Equal(g23,g22)
    c: Equal(g22,g21)
    c: Equal(g21,g20)
    c: Diameter(g20) = 49
    c: Coincident(g24,g25)
    c: Coincident(g25,g26)
    c: Coincident(g26,g27)
    c: Coincident(g27,g24)
    c: Vertical(g24)
    c: Vertical(g26)
    c: Horizontal(g25)
    c: Horizontal(g27)
    c: Symmetric(g26,g24,g28)
    c: Coincident(g28,g4)
    c: Coincident(g29,g30)
    c: Coincident(g30,g31)
    c: Coincident(g31,g32)
    c: Coincident(g32,g29)
    c: Vertical(g29)
    c: Vertical(g31)
    c: Horizontal(g30)
    c: Horizontal(g32)
    c: Symmetric(g31,g29,g33)
    c: Coincident(g33,g9)
    c: Coincident(g34,g35)
    c: Coincident(g35,g36)
    c: Coincident(g36,g37)
    c: Coincident(g37,g34)
    c: Vertical(g34)
    c: Vertical(g36)
    c: Horizontal(g35)
    c: Horizontal(g37)
    c: Symmetric(g36,g34,g38)
    c: Coincident(g38,g14)
    c: Coincident(g39,g40)
    c: Coincident(g40,g41)
    c: Coincident(g41,g42)
    c: Coincident(g42,g39)
    c: Vertical(g39)
    c: Vertical(g41)
    c: Horizontal(g40)
    c: Horizontal(g42)
    c: Symmetric(g41,g39,g43)
    c: Coincident(g43,g19)
    c: Equal(g40,g39)
    c: Equal(g39,g35)
    c: Equal(g35,g34)
    c: Equal(g34,g30)
    c: Equal(g30,g29)
    c: Equal(g29,g25)
    c: Equal(g25,g24)
    c: DistanceX(g25,g25) = 40
    c: Coincident(g44,g25)
    c: Coincident(g45,g24)
    c: Coincident(g46,g30)
    c: Coincident(g47,g26)
    c: Coincident(g48,g24)
    c: Coincident(g49,g31)
    c: Coincident(g50,g29)
    c: Coincident(g51,g36)
    c: Coincident(g52,g34)
    c: Coincident(g53,g41)
    c: Coincident(g54,g39)
    c: Coincident(g55,g39)
    c: Coincident(g56,g40)
    c: Coincident(g57,g34)
    c: Coincident(g58,g35)
    c: Coincident(g59,g29)
    c: Equal(g44,g45)
    c: Equal(g45,g46)
    c: Equal(g46,g47)
    c: Equal(g47,g48)
    c: Equal(g48,g49)
    c: Equal(g49,g50)
    c: Equal(g50,g51)
    c: Equal(g51,g52)
    c: Equal(g52,g53)
    c: Equal(g53,g54)
    c: Equal(g54,g55)
    c: Equal(g55,g56)
    c: Equal(g56,g57)
    c: Equal(g57,g58)
    c: Equal(g58,g59)
    c: Diameter(g47) = 3.5
    c: Distance(g1,g8) = 2
    c: Distance(g6,g13) = 2
    c: Distance(g11,g18) = 2
FEATURE [Sketcher::SketchObject] Sketch024  label="fanholes"
  ArcFitTolerance = 1e-06
  AttachmentSupport = -> [YZ_Plane015]
  FullyConstrained = true
  MakeInternals = false
  MapMode = 5
  Placement = pos=(0,0,0) rot=(0.57735,0.57735,0.57735;2.0944rad)
  expr: Constraints[104] = <<components>>.fan_spacing
  expr: Constraints[10] = <<choices>>.exit_height
  expr: Constraints[137] = <<choices>>.fan_gap
  expr: Constraints[138] = <<choices>>.fan_gap
  expr: Constraints[139] = <<choices>>.fan_gap
  expr: Constraints[21] = <<choices>>.exit_height
  expr: Constraints[32] = <<choices>>.exit_height
  expr: Constraints[43] = <<choices>>.exit_height
  expr: Constraints[56] = <<choices>>.exit_fan_dia
  sketch-geometry (60):
    g0: LineSegment [constr] StartX=4 StartY=0 StartZ=0 EndX=54 EndY=0 EndZ=0
    g1: LineSegment [constr] StartX=54 StartY=0 StartZ=0 EndX=54 EndY=55 EndZ=0
    g2: LineSegment [constr] StartX=54 StartY=55 StartZ=0 EndX=4 EndY=55 EndZ=0
    g3: LineSegment [constr] StartX=4 StartY=55 StartZ=0 EndX=4 EndY=0 EndZ=0
    g4: GeomPoint [constr] X=29 Y=27.5 Z=0
    g5: LineSegment [constr] StartX=56 StartY=0 StartZ=0 EndX=106 EndY=0 EndZ=0
    g6: LineSegment [constr] StartX=106 StartY=0 StartZ=0 EndX=106 EndY=55 EndZ=0
    g7: LineSegment [constr] StartX=106 StartY=55 StartZ=0 EndX=56 EndY=55 EndZ=0
    g8: LineSegment [constr] StartX=56 StartY=55 StartZ=0 EndX=56 EndY=0 EndZ=0
    g9: GeomPoint [constr] X=81 Y=27.5 Z=0
    g10: LineSegment [constr] StartX=108 StartY=0 StartZ=0 EndX=158 EndY=0 EndZ=0
    g11: LineSegment [constr] StartX=158 StartY=0 StartZ=0 EndX=158 EndY=55 EndZ=0
    g12: LineSegment [constr] StartX=158 StartY=55 StartZ=0 EndX=108 EndY=55 EndZ=0
    g13: LineSegment [constr] StartX=108 StartY=55 StartZ=0 EndX=108 EndY=0 EndZ=0
    g14: GeomPoint [constr] X=133 Y=27.5 Z=0
    g15: LineSegment [constr] StartX=160 StartY=0 StartZ=0 EndX=210 EndY=0 EndZ=0
    g16: LineSegment [constr] StartX=210 StartY=0 StartZ=0 EndX=210 EndY=55 EndZ=0
    g17: LineSegment [constr] StartX=210 StartY=55 StartZ=0 EndX=160 EndY=55 EndZ=0
    g18: LineSegment [constr] StartX=160 StartY=55 StartZ=0 EndX=160 EndY=0 EndZ=0
    g19: GeomPoint [constr] X=185 Y=27.5 Z=0
    g20: Circle [constr] CenterX=29 CenterY=27.5 CenterZ=0 NormalX=0 NormalY=0 NormalZ=1 AngleXU=0 Radius=24.5
    g21: Circle [constr] CenterX=81 CenterY=27.5 CenterZ=0 NormalX=0 NormalY=0 NormalZ=1 AngleXU=0 Radius=24.5
    g22: Circle [constr] CenterX=133 CenterY=27.5 CenterZ=0 NormalX=0 NormalY=0 NormalZ=1 AngleXU=0 Radius=24.5
    g23: Circle [constr] CenterX=185 CenterY=27.5 CenterZ=0 NormalX=0 NormalY=0 NormalZ=1 AngleXU=0 Radius=24.5
    g24: LineSegment [constr] StartX=49 StartY=7.5 StartZ=0 EndX=49 EndY=47.5 EndZ=0
    g25: LineSegment [constr] StartX=49 StartY=47.5 StartZ=0 EndX=9 EndY=47.5 EndZ=0
    g26: LineSegment [constr] StartX=9 StartY=47.5 StartZ=0 EndX=9 EndY=7.5 EndZ=0
    g27: LineSegment [constr] StartX=9 StartY=7.5 StartZ=0 EndX=49 EndY=7.5 EndZ=0
    g28: GeomPoint [constr] X=29 Y=27.5 Z=0
    g29: LineSegment [constr] StartX=101 StartY=7.5 StartZ=0 EndX=101 EndY=47.5 EndZ=0
    g30: LineSegment [constr] StartX=101 StartY=47.5 StartZ=0 EndX=61 EndY=47.5 EndZ=0
    g31: LineSegment [constr] StartX=61 StartY=47.5 StartZ=0 EndX=61 EndY=7.5 EndZ=0
    g32: LineSegment [constr] StartX=61 StartY=7.5 StartZ=0 EndX=101 EndY=7.5 EndZ=0
    g33: GeomPoint [constr] X=81 Y=27.5 Z=0
    g34: LineSegment [constr] StartX=153 StartY=7.5 StartZ=0 EndX=153 EndY=47.5 EndZ=0
    g35: LineSegment [constr] StartX=153 StartY=47.5 StartZ=0 EndX=113 EndY=47.5 EndZ=0
    g36: LineSegment [constr] StartX=113 StartY=47.5 StartZ=0 EndX=113 EndY=7.5 EndZ=0
    g37: LineSegment [constr] StartX=113 StartY=7.5 StartZ=0 EndX=153 EndY=7.5 EndZ=0
    g38: GeomPoint [constr] X=133 Y=27.5 Z=0
    g39: LineSegment [constr] StartX=205 StartY=7.5 StartZ=0 EndX=205 EndY=47.5 EndZ=0
    g40: LineSegment [constr] StartX=205 StartY=47.5 StartZ=0 EndX=165 EndY=47.5 EndZ=0
    g41: LineSegment [constr] StartX=165 StartY=47.5 StartZ=0 EndX=165 EndY=7.5 EndZ=0
    g42: LineSegment [constr] StartX=165 StartY=7.5 StartZ=0 EndX=205 EndY=7.5 EndZ=0
    g43: GeomPoint [constr] X=185 Y=27.5 Z=0
    g44: Circle CenterX=9 CenterY=47.5 CenterZ=0 NormalX=0 NormalY=0 NormalZ=1 AngleXU=0 Radius=1.5
    g45: Circle CenterX=49 CenterY=47.5 CenterZ=0 NormalX=0 NormalY=0 NormalZ=1 AngleXU=0 Radius=1.5
    g46: Circle CenterX=61 CenterY=47.5 CenterZ=0 NormalX=0 NormalY=0 NormalZ=1 AngleXU=0 Radius=1.5
    g47: Circle CenterX=9 CenterY=7.5 CenterZ=0 NormalX=0 NormalY=0 NormalZ=1 AngleXU=0 Radius=1.5
    g48: Circle CenterX=49 CenterY=7.5 CenterZ=0 NormalX=0 NormalY=0 NormalZ=1 AngleXU=0 Radius=1.5
    g49: Circle CenterX=61 CenterY=7.5 CenterZ=0 NormalX=0 NormalY=0 NormalZ=1 AngleXU=0 Radius=1.5
    g50: Circle CenterX=101 CenterY=7.5 CenterZ=0 NormalX=0 NormalY=0 NormalZ=1 AngleXU=0 Radius=1.5
    g51: Circle CenterX=113 CenterY=7.5 CenterZ=0 NormalX=0 NormalY=0 NormalZ=1 AngleXU=0 Radius=1.5
    g52: Circle CenterX=153 CenterY=7.5 CenterZ=0 NormalX=0 NormalY=0 NormalZ=1 AngleXU=0 Radius=1.5
    g53: Circle CenterX=165 CenterY=7.5 CenterZ=0 NormalX=0 NormalY=0 NormalZ=1 AngleXU=0 Radius=1.5
    g54: Circle CenterX=205 CenterY=7.5 CenterZ=0 NormalX=0 NormalY=0 NormalZ=1 AngleXU=0 Radius=1.5
    g55: Circle CenterX=205 CenterY=47.5 CenterZ=0 NormalX=0 NormalY=0 NormalZ=1 AngleXU=0 Radius=1.5
    g56: Circle CenterX=165 CenterY=47.5 CenterZ=0 NormalX=0 NormalY=0 NormalZ=1 AngleXU=0 Radius=1.5
    g57: Circle CenterX=153 CenterY=47.5 CenterZ=0 NormalX=0 NormalY=0 NormalZ=1 AngleXU=0 Radius=1.5
    g58: Circle CenterX=113 CenterY=47.5 CenterZ=0 NormalX=0 NormalY=0 NormalZ=1 AngleXU=0 Radius=1.5
    g59: Circle CenterX=101 CenterY=47.5 CenterZ=0 NormalX=0 NormalY=0 NormalZ=1 AngleXU=0 Radius=1.5
  constraints (140):
    c: Coincident(g0,g1)
    c: Coincident(g1,g2)
    c: Coincident(g2,g3)
    c: Coincident(g3,g0)
    c: Horizontal(g0)
    c: Horizontal(g2)
    c: Vertical(g1)
    c: Vertical(g3)
    c: Symmetric(g2,g0,g4)
    c: Distance(g1,g3) = 50
    c: Distance(g0,g2) = 55
    c: Coincident(g5,g6)
    c: Coincident(g6,g7)
    c: Coincident(g7,g8)
    c: Coincident(g8,g5)
    c: Horizontal(g5)
    c: Horizontal(g7)
    c: Vertical(g6)
    c: Vertical(g8)
    c: Symmetric(g7,g5,g9)
    c: Distance(g6,g8) = 50
    c: Distance(g5,g7) = 55
    c: Coincident(g10,g11)
    c: Coincident(g11,g12)
    c: Coincident(g12,g13)
    c: Coincident(g13,g10)
    c: Horizontal(g10)
    c: Horizontal(g12)
    c: Vertical(g11)
    c: Vertical(g13)
    c: Symmetric(g12,g10,g14)
    c: Distance(g11,g13) = 50
    c: Distance(g10,g12) = 55
    c: Coincident(g15,g16)
    c: Coincident(g16,g17)
    c: Coincident(g17,g18)
    c: Coincident(g18,g15)
    c: Horizontal(g15)
    c: Horizontal(g17)
    c: Vertical(g16)
    c: Vertical(g18)
    c: Symmetric(g17,g15,g19)
    c: Distance(g16,g18) = 50
    c: Distance(g15,g17) = 55
    c: PointOnObject(g0,g-1)
    c: PointOnObject(g5,g-1)
    c: PointOnObject(g10,g-1)
    c: PointOnObject(g15,g-1)
    c: DistanceX(g0) = 4
    c: Coincident(g20,g4)
    c: Coincident(g21,g9)
    c: Coincident(g22,g14)
    c: Coincident(g23,g19)
    c: Equal(g23,g22)
    c: Equal(g22,g21)
    c: Equal(g21,g20)
    c: Diameter(g20) = 49
    c: Coincident(g24,g25)
    c: Coincident(g25,g26)
    c: Coincident(g26,g27)
    c: Coincident(g27,g24)
    c: Vertical(g24)
    c: Vertical(g26)
    c: Horizontal(g25)
    c: Horizontal(g27)
    c: Symmetric(g26,g24,g28)
    c: Coincident(g28,g4)
    c: Coincident(g29,g30)
    c: Coincident(g30,g31)
    c: Coincident(g31,g32)
    c: Coincident(g32,g29)
    c: Vertical(g29)
    c: Vertical(g31)
    c: Horizontal(g30)
    c: Horizontal(g32)
    c: Symmetric(g31,g29,g33)
    c: Coincident(g33,g9)
    c: Coincident(g34,g35)
    c: Coincident(g35,g36)
    c: Coincident(g36,g37)
    c: Coincident(g37,g34)
    c: Vertical(g34)
    c: Vertical(g36)
    c: Horizontal(g35)
    c: Horizontal(g37)
    c: Symmetric(g36,g34,g38)
    c: Coincident(g38,g14)
    c: Coincident(g39,g40)
    c: Coincident(g40,g41)
    c: Coincident(g41,g42)
    c: Coincident(g42,g39)
    c: Vertical(g39)
    c: Vertical(g41)
    c: Horizontal(g40)
    c: Horizontal(g42)
    c: Symmetric(g41,g39,g43)
    c: Coincident(g43,g19)
    c: Equal(g40,g39)
    c: Equal(g39,g35)
    c: Equal(g35,g34)
    c: Equal(g34,g30)
    c: Equal(g30,g29)
    c: Equal(g29,g25)
    c: Equal(g25,g24)
    c: DistanceX(g25,g25) = 40
    c: Coincident(g44,g25)
    c: Coincident(g45,g24)
    c: Coincident(g46,g30)
    c: Coincident(g47,g26)
    c: Coincident(g48,g24)
    c: Coincident(g49,g31)
    c: Coincident(g50,g29)
    c: Coincident(g51,g36)
    c: Coincident(g52,g34)
    c: Coincident(g53,g41)
    c: Coincident(g54,g39)
    c: Coincident(g55,g39)
    c: Coincident(g56,g40)
    c: Coincident(g57,g34)
    c: Coincident(g58,g35)
    c: Coincident(g59,g29)
    c: Equal(g44,g45)
    c: Equal(g45,g46)
    c: Equal(g46,g47)
    c: Equal(g47,g48)
    c: Equal(g48,g49)
    c: Equal(g49,g50)
    c: Equal(g50,g51)
    c: Equal(g51,g52)
    c: Equal(g52,g53)
    c: Equal(g53,g54)
    c: Equal(g54,g55)
    c: Equal(g55,g56)
    c: Equal(g56,g57)
    c: Equal(g57,g58)
    c: Equal(g58,g59)
    c: Diameter(g47) = 3
    c: Distance(g1,g8) = 2
    c: Distance(g6,g13) = 2
    c: Distance(g11,g18) = 2
FEATURE [Sketcher::SketchObject] Sketch025
  ArcFitTolerance = 1e-06
  AttachmentSupport = -> [DatumPlane002]
  FullyConstrained = true
  MakeInternals = false
  MapMode = 5
  Placement = pos=(19,0,0) rot=(0.57735,0.57735,0.57735;2.0944rad)
  expr: Constraints[89] = <<choices>>.exit_vane_thinnest
  expr: Constraints[90] = <<choices>>.exit_height - <<choices>>.exit_vane_thinnest * 2
  expr: Constraints[91] = 3 + <<choices>>.exit_vane_thinnest
  expr: Constraints[92] = <<choices>>.exit_vane_thinnest
  expr: Constraints[93] = <<choices>>.exit_vane_thinnest
  expr: Constraints[94] = <<choices>>.exit_vane_thinnest
  expr: Constraints[95] = 50 + <<choices>>.fan_gap
  sketch-geometry (40):
    g0: LineSegment StartX=5 StartY=1 StartZ=0 EndX=54 EndY=1 EndZ=0
    g1: LineSegment StartX=55 StartY=2 StartZ=0 EndX=55 EndY=53 EndZ=0
    g2: LineSegment StartX=54 StartY=54 StartZ=0 EndX=5 EndY=54 EndZ=0
    g3: LineSegment StartX=4 StartY=53 StartZ=0 EndX=4 EndY=2 EndZ=0
    g4: ArcOfCircle CenterX=5 CenterY=2 CenterZ=0 NormalX=0 NormalY=0 NormalZ=1 AngleXU=0 Radius=1 StartAngle=3.14159 EndAngle=4.71239
    g5: ArcOfCircle CenterX=54 CenterY=2 CenterZ=0 NormalX=0 NormalY=0 NormalZ=1 AngleXU=0 Radius=1 StartAngle=4.71239 EndAngle=6.28319
    g6: ArcOfCircle CenterX=54 CenterY=53 CenterZ=0 NormalX=0 NormalY=0 NormalZ=1 AngleXU=0 Radius=1 StartAngle=0 EndAngle=1.5708
    g7: ArcOfCircle CenterX=5 CenterY=53 CenterZ=0 NormalX=0 NormalY=0 NormalZ=1 AngleXU=0 Radius=1 StartAngle=1.5708 EndAngle=3.14159
    g8: GeomPoint [constr] X=4 Y=1 Z=0
    g9: GeomPoint [constr] X=55 Y=54 Z=0
    g10: LineSegment StartX=56 StartY=53 StartZ=0 EndX=56 EndY=2 EndZ=0
    g11: LineSegment StartX=57 StartY=1 StartZ=0 EndX=106 EndY=1 EndZ=0
    g12: LineSegment StartX=107 StartY=2 StartZ=0 EndX=107 EndY=53 EndZ=0
    g13: LineSegment StartX=106 StartY=54 StartZ=0 EndX=57 EndY=54 EndZ=0
    g14: ArcOfCircle CenterX=57 CenterY=53 CenterZ=0 NormalX=0 NormalY=0 NormalZ=1 AngleXU=0 Radius=1 StartAngle=1.5708 EndAngle=3.14159
    g15: ArcOfCircle CenterX=57 CenterY=2 CenterZ=0 NormalX=0 NormalY=0 NormalZ=1 AngleXU=0 Radius=1 StartAngle=3.14159 EndAngle=4.71239
    g16: ArcOfCircle CenterX=106 CenterY=2 CenterZ=0 NormalX=0 NormalY=0 NormalZ=1 AngleXU=0 Radius=1 StartAngle=4.71239 EndAngle=6.28319
    g17: ArcOfCircle CenterX=106 CenterY=53 CenterZ=0 NormalX=0 NormalY=0 NormalZ=1 AngleXU=0 Radius=1 StartAngle=-9e-16 EndAngle=1.5708
    g18: GeomPoint [constr] X=56 Y=54 Z=0
    g19: GeomPoint [constr] X=107 Y=1 Z=0
    g20: LineSegment StartX=109 StartY=1 StartZ=0 EndX=158 EndY=1 EndZ=0
    g21: LineSegment StartX=159 StartY=2 StartZ=0 EndX=159 EndY=53 EndZ=0
    g22: LineSegment StartX=158 StartY=54 StartZ=0 EndX=109 EndY=54 EndZ=0
    g23: LineSegment StartX=108 StartY=53 StartZ=0 EndX=108 EndY=2 EndZ=0
    g24: ArcOfCircle CenterX=109 CenterY=2 CenterZ=0 NormalX=0 NormalY=0 NormalZ=1 AngleXU=0 Radius=1 StartAngle=3.14159 EndAngle=4.71239
    g25: ArcOfCircle CenterX=158 CenterY=2 CenterZ=0 NormalX=0 NormalY=0 NormalZ=1 AngleXU=0 Radius=1 StartAngle=4.71239 EndAngle=6.28319
    g26: ArcOfCircle CenterX=158 CenterY=53 CenterZ=0 NormalX=0 NormalY=0 NormalZ=1 AngleXU=0 Radius=1 StartAngle=-1.8e-15 EndAngle=1.5708
    g27: ArcOfCircle CenterX=109 CenterY=53 CenterZ=0 NormalX=0 NormalY=0 NormalZ=1 AngleXU=0 Radius=1 StartAngle=1.5708 EndAngle=3.14159
    g28: GeomPoint [constr] X=108 Y=1 Z=0
    g29: GeomPoint [constr] X=159 Y=54 Z=0
    g30: LineSegment StartX=160 StartY=53 StartZ=0 EndX=160 EndY=2 EndZ=0
    g31: LineSegment StartX=161 StartY=1 StartZ=0 EndX=210 EndY=1 EndZ=0
    g32: LineSegment StartX=211 StartY=2 StartZ=0 EndX=211 EndY=53 EndZ=0
    g33: LineSegment StartX=210 StartY=54 StartZ=0 EndX=161 EndY=54 EndZ=0
    g34: ArcOfCircle CenterX=161 CenterY=53 CenterZ=0 NormalX=0 NormalY=0 NormalZ=1 AngleXU=0 Radius=1 StartAngle=1.5708 EndAngle=3.14159
    g35: ArcOfCircle CenterX=161 CenterY=2 CenterZ=0 NormalX=0 NormalY=0 NormalZ=1 AngleXU=0 Radius=1 StartAngle=3.14159 EndAngle=4.71239
    g36: ArcOfCircle CenterX=210 CenterY=2 CenterZ=0 NormalX=0 NormalY=0 NormalZ=1 AngleXU=0 Radius=1 StartAngle=4.71239 EndAngle=6.28319
    g37: ArcOfCircle CenterX=210 CenterY=53 CenterZ=0 NormalX=0 NormalY=0 NormalZ=1 AngleXU=0 Radius=1 StartAngle=1.9e-15 EndAngle=1.5708
    g38: GeomPoint [constr] X=160 Y=54 Z=0
    g39: GeomPoint [constr] X=211 Y=1 Z=0
  constraints (96):
    c: Tangent(g0,g4) = -1.5708
    c: Tangent(g0,g5) = -1.5708
    c: Tangent(g1,g5) = -1.5708
    c: Tangent(g1,g6) = -1.5708
    c: Tangent(g2,g6) = -1.5708
    c: Tangent(g2,g7) = -1.5708
    c: Tangent(g3,g7) = -1.5708
    c: Tangent(g3,g4) = -1.5708
    c: Horizontal(g0)
    c: Horizontal(g2)
    c: Vertical(g1)
    c: Vertical(g3)
    c: Equal(g4,g5)
    c: Equal(g5,g6)
    c: Equal(g6,g7)
    c: PointOnObject(g8,g0)
    c: PointOnObject(g8,g3)
    c: PointOnObject(g9,g1)
    c: PointOnObject(g9,g2)
    c: Tangent(g10,g14) = -1.5708
    c: Tangent(g10,g15) = -1.5708
    c: Tangent(g11,g15) = -1.5708
    c: Tangent(g11,g16) = -1.5708
    c: Tangent(g12,g16) = -1.5708
    c: Tangent(g12,g17) = -1.5708
    c: Tangent(g13,g17) = -1.5708
    c: Tangent(g13,g14) = -1.5708
    c: Vertical(g10)
    c: Vertical(g12)
    c: Horizontal(g11)
    c: Horizontal(g13)
    c: Equal(g14,g15)
    c: Equal(g15,g16)
    c: Equal(g16,g17)
    c: PointOnObject(g18,g10)
    c: PointOnObject(g18,g13)
    c: PointOnObject(g19,g11)
    c: PointOnObject(g19,g12)
    c: Tangent(g20,g24) = -1.5708
    c: Tangent(g20,g25) = -1.5708
    c: Tangent(g21,g25) = -1.5708
    c: Tangent(g21,g26) = -1.5708
    c: Tangent(g22,g26) = -1.5708
    c: Tangent(g22,g27) = -1.5708
    c: Tangent(g23,g27) = -1.5708
    c: Tangent(g23,g24) = -1.5708
    c: Horizontal(g20)
    c: Horizontal(g22)
    c: Vertical(g21)
    c: Vertical(g23)
    c: Equal(g24,g25)
    c: Equal(g25,g26)
    c: Equal(g26,g27)
    c: PointOnObject(g28,g20)
    c: PointOnObject(g28,g23)
    c: PointOnObject(g29,g21)
    c: PointOnObject(g29,g22)
    c: Tangent(g30,g34) = -1.5708
    c: Tangent(g30,g35) = -1.5708
    c: Tangent(g31,g35) = -1.5708
    c: Tangent(g31,g36) = -1.5708
    c: Tangent(g32,g36) = -1.5708
    c: Tangent(g32,g37) = -1.5708
    c: Tangent(g33,g37) = -1.5708
    c: Tangent(g33,g34) = -1.5708
    c: Vertical(g30)
    c: Vertical(g32)
    c: Horizontal(g31)
    c: Horizontal(g33)
    c: Equal(g34,g35)
    c: Equal(g35,g36)
    c: Equal(g36,g37)
    c: PointOnObject(g38,g30)
    c: PointOnObject(g38,g33)
    c: PointOnObject(g39,g31)
    c: PointOnObject(g39,g32)
    c: Equal(g7,g14)
    c: Equal(g14,g27)
    c: Equal(g27,g34)
    c: Radius(g34) = 1
    c: Equal(g2,g13)
    c: Equal(g13,g22)
    c: Equal(g22,g33)
    c: Equal(g1,g10)
    c: Equal(g10,g23)
    c: Equal(g23,g30)
    c: PointOnObject(g11,g0)
    c: PointOnObject(g20,g11)
    c: PointOnObject(g31,g20)
    c: DistanceY(g0) = 1
    c: Distance(g2,g0) = 53
    c: DistanceX(g3) = 4
    c: Distance(g1,g10) = 1
    c: Distance(g12,g23) = 1
    c: Distance(g29,g30) = 1
    c: Distance(g3,g10) = 52
FEATURE [Sketcher::SketchObject] Sketch026
  ArcFitTolerance = 1e-06
  AttachmentSupport = -> [DatumPlane002]
  FullyConstrained = true
  MakeInternals = false
  MapMode = 5
  Placement = pos=(19,0,0) rot=(0.57735,0.57735,0.57735;2.0944rad)
  expr: Constraints[31] = 4 - 0.5 * <<choices>>.fan_gap
  expr: Constraints[32] = <<choices>>.exit_vane_thinnest
  expr: Constraints[34] = <<choices>>.exit_height
  expr: Constraints[35] = 50 + <<choices>>.fan_gap
  sketch-geometry (12):
    g0: LineSegment StartX=3 StartY=27 StartZ=0 EndX=28.5 EndY=27 EndZ=0
    g1: LineSegment StartX=28.5 StartY=27 StartZ=0 EndX=28.5 EndY=0 EndZ=0
    g2: LineSegment StartX=28.5 StartY=0 StartZ=0 EndX=29.5 EndY=0 EndZ=0
    g3: LineSegment StartX=29.5 StartY=0 StartZ=0 EndX=29.5 EndY=27 EndZ=0
    g4: LineSegment StartX=29.5 StartY=27 StartZ=0 EndX=55 EndY=27 EndZ=0
    g5: LineSegment StartX=55 StartY=27 StartZ=0 EndX=55 EndY=28 EndZ=0
    g6: LineSegment StartX=55 StartY=28 StartZ=0 EndX=29.5 EndY=28 EndZ=0
    g7: LineSegment StartX=29.5 StartY=28 StartZ=0 EndX=29.5 EndY=55 EndZ=0
    g8: LineSegment StartX=29.5 StartY=55 StartZ=0 EndX=28.5 EndY=55 EndZ=0
    g9: LineSegment StartX=28.5 StartY=55 StartZ=0 EndX=28.5 EndY=28 EndZ=0
    g10: LineSegment StartX=28.5 StartY=28 StartZ=0 EndX=3 EndY=28 EndZ=0
    g11: LineSegment StartX=3 StartY=28 StartZ=0 EndX=3 EndY=27 EndZ=0
  constraints (36):
    c: Horizontal(g0)
    c: Coincident(g0,g1)
    c: Vertical(g1)
    c: Coincident(g1,g2)
    c: PointOnObject(g2,g-1)
    c: Horizontal(g2)
    c: Coincident(g2,g3)
    c: Vertical(g3)
    c: Coincident(g3,g4)
    c: Horizontal(g4)
    c: Coincident(g4,g5)
    c: Vertical(g5)
    c: Coincident(g5,g6)
    c: Horizontal(g6)
    c: Coincident(g6,g7)
    c: Vertical(g7)
    c: Coincident(g7,g8)
    c: Horizontal(g8)
    c: Coincident(g8,g9)
    c: Vertical(g9)
    c: Coincident(g9,g10)
    c: Horizontal(g10)
    c: Coincident(g10,g11)
    c: Coincident(g11,g0)
    c: Vertical(g11)
    c: Equal(g10,g0)
    c: Equal(g6,g4)
    c: Equal(g4,g0)
    c: Equal(g7,g9)
    c: Equal(g9,g1)
    c: Equal(g1,g3)
    c: DistanceX(g0) = 3
    c: DistanceY(g11,g11) = 1
    c: Equal(g2,g5)
    c: DistanceY(g7) = 55
    c: Distance(g5,g11) = 52
FEATURE [Sketcher::SketchObject] Sketch027
  ArcFitTolerance = 1e-06
  AttachmentSupport = -> [YZ_Plane015]
  FullyConstrained = true
  MakeInternals = false
  MapMode = 5
  Placement = pos=(0,0,0) rot=(0.57735,0.57735,0.57735;2.0944rad)
  expr: Constraints[20] = <<choices>>.exit_height / 2
  expr: Constraints[22] = <<choices>>.exit_cone
  expr: Constraints[24] = <<choices>>.exit_height
  expr: Constraints[31] = <<choices>>.exit_vane_thickest
  expr: Constraints[49] = <<choices>>.exit_vane_thickest
  sketch-geometry (16):
    g0: ArcOfCircle CenterX=29 CenterY=27.5 CenterZ=0 NormalX=0 NormalY=0 NormalZ=1 AngleXU=0 Radius=12.25 StartAngle=3.26435 EndAngle=4.58963
    g1: LineSegment StartX=4 StartY=29 StartZ=0 EndX=16.8422 EndY=29 EndZ=0
    g2: LineSegment StartX=4 StartY=29 StartZ=0 EndX=4 EndY=26 EndZ=0
    g3: LineSegment StartX=4 StartY=26 StartZ=0 EndX=16.8422 EndY=26 EndZ=0
    g4: LineSegment StartX=27.5 StartY=15.3422 StartZ=0 EndX=27.5 EndY=0 EndZ=0
    g5: LineSegment StartX=27.5 StartY=0 StartZ=0 EndX=30.5 EndY=0 EndZ=0
    g6: LineSegment StartX=30.5 StartY=0 StartZ=0 EndX=30.5 EndY=15.3422 EndZ=0
    g7: LineSegment StartX=41.1578 StartY=26 StartZ=0 EndX=55 EndY=26 EndZ=0
    g8: LineSegment StartX=55 StartY=26 StartZ=0 EndX=55 EndY=29 EndZ=0
    g9: LineSegment StartX=55 StartY=29 StartZ=0 EndX=41.1578 EndY=29 EndZ=0
    g10: LineSegment StartX=30.5 StartY=39.6578 StartZ=0 EndX=30.5 EndY=55 EndZ=0
    g11: LineSegment StartX=30.5 StartY=55 StartZ=0 EndX=27.5 EndY=55 EndZ=0
    g12: LineSegment StartX=27.5 StartY=55 StartZ=0 EndX=27.5 EndY=39.6578 EndZ=0
    g13: ArcOfCircle CenterX=29 CenterY=27.5 CenterZ=0 NormalX=0 NormalY=0 NormalZ=1 AngleXU=0 Radius=12.25 StartAngle=4.83515 EndAngle=6.16043
    g14: ArcOfCircle CenterX=29 CenterY=27.5 CenterZ=0 NormalX=0 NormalY=0 NormalZ=1 AngleXU=0 Radius=12.25 StartAngle=1.69355 EndAngle=3.01884
    g15: ArcOfCircle CenterX=29 CenterY=27.5 CenterZ=0 NormalX=0 NormalY=0 NormalZ=1 AngleXU=0 Radius=12.25 StartAngle=0.122757 EndAngle=1.44804
  constraints (50):
    c: Horizontal(g1)
    c: Coincident(g1,g2)
    c: Vertical(g2)
    c: Coincident(g2,g3)
    c: Horizontal(g3)
    c: PointOnObject(g4,g-1)
    c: Vertical(g4)
    c: Coincident(g4,g5)
    c: PointOnObject(g5,g-1)
    c: Coincident(g5,g6)
    c: PointOnObject(g6,g13)
    c: Horizontal(g7)
    c: Coincident(g7,g8)
    c: Vertical(g8)
    c: Coincident(g8,g9)
    c: Horizontal(g9)
    c: Vertical(g10)
    c: Coincident(g10,g11)
    c: Coincident(g11,g12)
    c: Vertical(g12)
    c: DistanceY(g0) = 27.5
    c: DistanceX(g0) = 29
    c: Diameter(g0) = 24.5
    c: Horizontal(g11)
    c: DistanceY(g11) = 55
    c: Vertical(g6)
    c: Symmetric(g6,g12,g0)
    c: PointOnObject(g12,g4)
    c: PointOnObject(g6,g10)
    c: PointOnObject(g9,g1)
    c: PointOnObject(g3,g7)
    c: Distance(g1,g3) = 3
    c: Symmetric(g3,g9,g0)
    c: DistanceX(g2) = 4
    c: DistanceX(g7) = 55
    c: Coincident(g14,g1)
    c: Coincident(g0,g3)
    c: Equal(g0,g13)
    c: Coincident(g0,g4)
    c: PointOnObject(g13,g6)
    c: Coincident(g0,g13)
    c: Equal(g13,g14)
    c: Coincident(g15,g10)
    c: PointOnObject(g14,g12)
    c: Coincident(g13,g14)
    c: Equal(g13,g15)
    c: Coincident(g13,g7)
    c: PointOnObject(g15,g9)
    c: Coincident(g13,g15)
    c: Distance(g5) = 3
FEATURE [Sketcher::SketchObject] Sketch028
  ArcFitTolerance = 1e-06
  AttachmentSupport = -> [DatumPlane002]
  FullyConstrained = false
  MakeInternals = false
  MapMode = 5
  Placement = pos=(19,0,0) rot=(0.57735,0.57735,0.57735;2.0944rad)
  expr: Constraints[7] = <<components>>.frame_h - 12.5
  sketch-geometry (15):
    g0: ArcOfCircle CenterX=229.5 CenterY=40 CenterZ=0 NormalX=0 NormalY=0 NormalZ=1 AngleXU=0 Radius=3.5 StartAngle=4.71239 EndAngle=7.85398
    g1: ArcOfCircle CenterX=217 CenterY=40 CenterZ=0 NormalX=0 NormalY=0 NormalZ=1 AngleXU=0 Radius=3.5 StartAngle=1.5708 EndAngle=4.71239
    g2: LineSegment StartX=229.5 StartY=36.5 StartZ=0 EndX=217 EndY=36.5 EndZ=0
    g3: LineSegment StartX=229.5 StartY=43.5 StartZ=0 EndX=217 EndY=43.5 EndZ=0
    g4: LineSegment [constr] StartX=217 StartY=40 StartZ=0 EndX=217 EndY=56.7823 EndZ=0
    g5: LineSegment [constr] StartX=229.5 StartY=40 StartZ=0 EndX=229.5 EndY=56.7823 EndZ=0
    g6: LineSegment [constr] StartX=229.5 StartY=56.7823 StartZ=0 EndX=217 EndY=56.7823 EndZ=0
    g7: ArcOfCircle CenterX=217 CenterY=25 CenterZ=0 NormalX=0 NormalY=0 NormalZ=1 AngleXU=0 Radius=3.5 StartAngle=1.5708 EndAngle=4.71239
    g8: ArcOfCircle CenterX=229.5 CenterY=25 CenterZ=0 NormalX=0 NormalY=0 NormalZ=1 AngleXU=0 Radius=3.5 StartAngle=4.71239 EndAngle=7.85398
    g9: LineSegment StartX=217 StartY=28.5 StartZ=0 EndX=229.5 EndY=28.5 EndZ=0
    g10: LineSegment StartX=217 StartY=21.5 StartZ=0 EndX=229.5 EndY=21.5 EndZ=0
    g11: ArcOfCircle [constr] CenterX=217 CenterY=40 CenterZ=0 NormalX=0 NormalY=0 NormalZ=1 AngleXU=0 Radius=2.5 StartAngle=1.5708 EndAngle=4.71239
    g12: ArcOfCircle [constr] CenterX=229.5 CenterY=40 CenterZ=0 NormalX=0 NormalY=0 NormalZ=1 AngleXU=0 Radius=2.5 StartAngle=4.71239 EndAngle=7.85398
    g13: LineSegment [constr] StartX=217 StartY=42.5 StartZ=0 EndX=229.5 EndY=42.5 EndZ=0
    g14: LineSegment [constr] StartX=217 StartY=37.5 StartZ=0 EndX=229.5 EndY=37.5 EndZ=0
  constraints (37):
    c: Tangent(g0,g2) = 1.5708
    c: Tangent(g0,g3) = -1.5708
    c: Tangent(g1,g2) = 1.5708
    c: Tangent(g1,g3) = -1.5708
    c: Equal(g0,g1)
    c: Radius(g0) = 3.5
    c: Horizontal(g2)
    c: DistanceX(g1) = 217
    c: DistanceY(g1) = 40
    c: Coincident(g4,g1)
    c: Vertical(g4)
    c: Coincident(g5,g0)
    c: Vertical(g5)
    c: Coincident(g6,g5)
    c: Coincident(g6,g4)
    c: Horizontal(g6)
    c: Tangent(g7,g9) = 1.5708
    c: Tangent(g7,g10) = -1.5708
    c: Tangent(g8,g9) = 1.5708
    c: Tangent(g8,g10) = -1.5708
    c: Equal(g7,g8)
    c: Radius(g7) = 3.5
    c: PointOnObject(g7,g4)
    c: PointOnObject(g8,g5)
    c: Horizontal(g9)
    c: Tangent(g11,g13) = 1.5708
    c: Tangent(g11,g14) = -1.5708
    c: Tangent(g12,g13) = 1.5708
    c: Tangent(g12,g14) = -1.5708
    c: Equal(g11,g12)
    c: Horizontal(g14)
    c: Radius(g11) = 2.5
    c: PointOnObject(g11,g4)
    c: PointOnObject(g12,g5)
    c: DistanceY(g7) = 25
    c: DistanceY(g11) = 40
    c: DistanceX(g6,g6) = 12.5
FEATURE [Sketcher::SketchObject] Sketch036
  ArcFitTolerance = 1e-06
  AttachmentSupport = -> [YZ_Plane015]
  FullyConstrained = true
  MakeInternals = false
  MapMode = 5
  Placement = pos=(0,0,0) rot=(0.57735,0.57735,0.57735;2.0944rad)
  expr: Constraints[10] = <<components>>.frame_h
  expr: Constraints[32] = 4 + 4 * <<components>>.fan_h + 4 * <<choices>>.fan_gap
  expr: Constraints[9] = <<choices>>.exit_height
  sketch-geometry (12):
    g0: LineSegment [constr] StartX=0 StartY=0 StartZ=0 EndX=229.5 EndY=0 EndZ=0
    g1: LineSegment [constr] StartX=229.5 StartY=0 StartZ=0 EndX=229.5 EndY=55 EndZ=0
    g2: LineSegment [constr] StartX=229.5 StartY=55 StartZ=0 EndX=0 EndY=55 EndZ=0
    g3: LineSegment [constr] StartX=0 StartY=55 StartZ=0 EndX=0 EndY=0 EndZ=0
    g4: LineSegment StartX=229.5 StartY=0 StartZ=0 EndX=229.5 EndY=55 EndZ=0
    g5: LineSegment StartX=229.5 StartY=55 StartZ=0 EndX=212 EndY=55 EndZ=0
    g6: LineSegment StartX=212 StartY=55 StartZ=0 EndX=212 EndY=0 EndZ=0
    g7: LineSegment StartX=212 StartY=0 StartZ=0 EndX=229.5 EndY=0 EndZ=0
    g8: LineSegment StartX=0 StartY=0 StartZ=0 EndX=3 EndY=0 EndZ=0
    g9: LineSegment StartX=3 StartY=0 StartZ=0 EndX=3 EndY=55 EndZ=0
    g10: LineSegment StartX=3 StartY=55 StartZ=0 EndX=0 EndY=55 EndZ=0
    g11: LineSegment StartX=0 StartY=55 StartZ=0 EndX=0 EndY=0 EndZ=0
  constraints (33):
    c: Coincident(g0,g1)
    c: Coincident(g1,g2)
    c: Coincident(g2,g3)
    c: Coincident(g3,g0)
    c: Horizontal(g0)
    c: Horizontal(g2)
    c: Vertical(g1)
    c: Vertical(g3)
    c: Coincident(g0,g-1)
    c: DistanceY(g1,g1) = 55
    c: DistanceX(g1) = 229.5
    c: Coincident(g4,g5)
    c: Coincident(g5,g6)
    c: Coincident(g6,g7)
    c: Coincident(g7,g4)
    c: Vertical(g4)
    c: Vertical(g6)
    c: Horizontal(g5)
    c: Horizontal(g7)
    c: Coincident(g4,g0)
    c: PointOnObject(g5,g2)
    c: Coincident(g8,g9)
    c: Coincident(g9,g10)
    c: Coincident(g10,g11)
    c: Coincident(g11,g8)
    c: Horizontal(g8)
    c: Horizontal(g10)
    c: Vertical(g9)
    c: Vertical(g11)
    c: Coincident(g8,g0)
    c: PointOnObject(g9,g2)
    c: DistanceX(g9) = 3
    c: DistanceX(g5) = 212
FEATURE [PartDesign::Pad] Pad021
  BaseFeature = -> Pad012
  Direction = (1,0,0)
  Length = 46
  Length2 = 10
  Profile = -> Sketch036
  ReferenceAxis = -> Sketch036 [N_Axis]
  Refine = true
  Reversed = true
  Suppressed = false
  Type = 0
  expr: Length = 65 - <<choices>>.exit_w
FEATURE [PartDesign::Plane] DatumPlane003
  AttachmentOffset = pos=(0,0,-25) rot=(0,0,1;0rad)
  AttachmentSupport = -> [YZ_Plane015]
  Length = 283.038
  MapMode = 5
  Placement = pos=(-25,0,0) rot=(0.57735,0.57735,0.57735;2.0944rad)
  ResizeMode = 0
  Width = 108.538
FEATURE [PartDesign::Plane] DatumPlane004
  AttachmentOffset = pos=(0,0,-47) rot=(0,0,1;0rad)
  AttachmentSupport = -> [YZ_Plane015]
  Length = 283.038
  MapMode = 5
  Placement = pos=(-47,0,0) rot=(0.57735,0.57735,0.57735;2.0944rad)
  ResizeMode = 0
  Width = 108.538
FEATURE [Sketcher::SketchObject] Sketch041
  ArcFitTolerance = 1e-06
  AttachmentSupport = -> [DatumPlane004]
  FullyConstrained = false
  MakeInternals = false
  MapMode = 5
  Placement = pos=(-47,0,0) rot=(0.57735,0.57735,0.57735;2.0944rad)
  expr: Constraints[9] = <<choices>>.base_max_thickness - 3
  sketch-geometry (4):
    g0: LineSegment StartX=0 StartY=0 StartZ=0 EndX=453.094 EndY=0 EndZ=0
    g1: LineSegment StartX=453.094 StartY=0 StartZ=0 EndX=453.094 EndY=17 EndZ=0
    g2: LineSegment StartX=453.094 StartY=17 StartZ=0 EndX=0 EndY=17 EndZ=0
    g3: LineSegment StartX=0 StartY=17 StartZ=0 EndX=0 EndY=0 EndZ=0
  constraints (10):
    c: Coincident(g0,g1)
    c: Coincident(g1,g2)
    c: Coincident(g2,g3)
    c: Coincident(g3,g0)
    c: Horizontal(g0)
    c: Horizontal(g2)
    c: Vertical(g1)
    c: Vertical(g3)
    c: Coincident(g0,g-1)
    c: DistanceY(g3,g3) = 17
FEATURE [Sketcher::SketchObject] Sketch043
  ArcFitTolerance = 1e-06
  AttachmentSupport = -> [XY_Plane015]
  FullyConstrained = false
  MakeInternals = false
  MapMode = 5
  expr: Constraints[10] = <<choices>>.shroud_mb_space + <<components>>.fan_w
  expr: Constraints[22] = <<components>>.fan_w
  expr: Constraints[26] = 4 + 4 * <<components>>.fan_h + 4 * <<choices>>.fan_gap
  expr: Constraints[9] = <<components>>.frame_h
  sketch-geometry (12):
    g0: LineSegment [constr] StartX=0 StartY=229.5 StartZ=0 EndX=-46 EndY=229.5 EndZ=0
    g1: LineSegment [constr] StartX=-46 StartY=229.5 StartZ=0 EndX=-46 EndY=0 EndZ=0
    g2: LineSegment [constr] StartX=-46 StartY=0 StartZ=0 EndX=0 EndY=0 EndZ=0
    g3: LineSegment [constr] StartX=0 StartY=0 StartZ=0 EndX=0 EndY=229.5 EndZ=0
    g4: LineSegment StartX=-46 StartY=224.5 StartZ=0 EndX=0 EndY=224.5 EndZ=0
    g5: LineSegment StartX=0 StartY=224.5 StartZ=0 EndX=0 EndY=212 EndZ=0
    g6: LineSegment StartX=0 StartY=212 StartZ=0 EndX=-17 EndY=212 EndZ=0
    g7: LineSegment StartX=-17 StartY=212 StartZ=0 EndX=-24.2296 EndY=209.005 EndZ=0
    g8: LineSegment StartX=-46 StartY=185 StartZ=0 EndX=-46 EndY=224.5 EndZ=0
    g9: LineSegment StartX=-37.554 StartY=195.681 StartZ=0 EndX=-24.2296 EndY=209.005 EndZ=0
    g10: LineSegment StartX=-46 StartY=185 StartZ=0 EndX=-43 EndY=185 EndZ=0
    g11: LineSegment StartX=-43 StartY=185 StartZ=0 EndX=-37.554 EndY=195.681 EndZ=0
  constraints (33):
    c: Coincident(g0,g1)
    c: Coincident(g1,g2)
    c: Coincident(g2,g3)
    c: Coincident(g3,g0)
    c: Horizontal(g0)
    c: Horizontal(g2)
    c: Vertical(g1)
    c: Vertical(g3)
    c: Coincident(g2,g-1)
    c: DistanceY(g1,g1) = 229.5
    c: DistanceX(g0,g0) = 46
    c: PointOnObject(g4,g1)
    c: PointOnObject(g4,g3)
    c: Horizontal(g4)
    c: Coincident(g4,g5)
    c: PointOnObject(g5,g3)
    c: Coincident(g5,g6)
    c: Horizontal(g6)
    c: Coincident(g6,g7)
    c: PointOnObject(g8,g1)
    c: Coincident(g8,g4)
    c: Distance(g4,g0) = 5
    c: DistanceX(g6,g6) = 17
    c: Angle(g7) = -2.74889
    c: Coincident(g9,g7)
    c: Angle(g9) = 0.785398
    c: DistanceY(g5) = 212
    c: Coincident(g8,g10)
    c: Horizontal(g10)
    c: Coincident(g10,g11)
    c: Coincident(g11,g9)
    c: DistanceY(g10) = 185
    c: DistanceX(g10,g10) = 3
FEATURE [PartDesign::Pad] Pad023
  BaseFeature = -> Pad021
  Direction = (0,0,1)
  Length = 55
  Length2 = 10
  Profile = -> Sketch043
  ReferenceAxis = -> Sketch043 [N_Axis]
  Refine = true
  Suppressed = false
  Type = 0
  expr: Length = <<choices>>.exit_height
FEATURE [PartDesign::Fillet] Fillet
  Base = -> Pad023 [Edge24]
  BaseFeature = -> Pad023
  Radius = 1
  Refine = true
  SupportTransform = false
  Suppressed = false
  UseAllEdges = false
  expr: Radius = <<choices>>.corner
FEATURE [PartDesign::Pocket] Pocket008
  BaseFeature = -> Fillet
  Direction = (-1,0,0)
  Length = 5
  Length2 = 5
  Midplane = true
  Profile = -> Sketch022
  ReferenceAxis = -> Sketch022 [N_Axis]
  Refine = true
  Suppressed = false
  Type = 1
FEATURE [PartDesign::SubtractiveLoft] SubtractiveLoft
  BaseFeature = -> Pocket008
  Closed = false
  Profile = -> Sketch023
  Refine = true
  Ruled = false
  Sections = -> [Sketch025]
  Suppressed = false
FEATURE [PartDesign::AdditiveLoft] AdditiveLoft
  BaseFeature = -> SubtractiveLoft
  Closed = false
  Profile = -> Sketch026
  Refine = true
  Ruled = false
  Sections = -> [Sketch027]
  Suppressed = false
FEATURE [PartDesign::LinearPattern] LinearPattern001
  BaseFeature = -> AdditiveLoft
  Direction = -> Sketch026 [H_Axis]
  Length = 156
  Mode = 1
  Occurrences = 4
  Offset = 52
  Originals = -> [AdditiveLoft]
  Refine = true
  Suppressed = false
  TransformMode = 0
  expr: Offset = <<choices>>.fan_gap + 50
FEATURE [PartDesign::Pocket] Pocket011
  BaseFeature = -> LinearPattern001
  Direction = (-1,0,0)
  Length = 3.9
  Length2 = 5
  Profile = -> Sketch041
  ReferenceAxis = -> Sketch041 [N_Axis]
  Refine = true
  Reversed = true
  Suppressed = false
  Type = 0
FEATURE [Sketcher::SketchObject] Sketch044  label="bottom plate screwholes"
  ArcFitTolerance = 1e-06
  AttachmentSupport = -> [XY_Plane015]
  FullyConstrained = false
  MakeInternals = false
  MapMode = 5
  expr: Constraints[10] = <<choices>>.screwhole_edge_margin + 3
  expr: Constraints[11] = <<choices>>.exit_w - <<choices>>.screwhole_edge_margin
  expr: Constraints[14] = <<components>>.m3_hole
  expr: Constraints[16] = <<components>>.m3_insert_r
  expr: Constraints[23] = <<components>>.fan_w + <<choices>>.exit_w + <<choices>>.shroud_mb_space - 2 * <<choices>>.screwhole_edge_margin - 3
  expr: Constraints[5] = <<components>>.frame_h
  expr: Constraints[6] = <<choices>>.screwhole_edge_margin + 3
  sketch-geometry (9):
    g0: Circle CenterX=14 CenterY=8 CenterZ=0 NormalX=0 NormalY=0 NormalZ=1 AngleXU=0 Radius=1.75
    g1: Circle CenterX=14 CenterY=221.5 CenterZ=0 NormalX=0 NormalY=0 NormalZ=1 AngleXU=0 Radius=3
    g2: LineSegment [constr] StartX=14 StartY=221.5 StartZ=0 EndX=14 EndY=8 EndZ=0
    g3: LineSegment [constr] StartX=-60.7131 StartY=0 StartZ=0 EndX=-60.7131 EndY=229.5 EndZ=0
    g4: LineSegment [constr] StartX=14 StartY=221.5 StartZ=0 EndX=-60.7131 EndY=221.5 EndZ=0
    g5: Circle CenterX=14 CenterY=114.75 CenterZ=0 NormalX=0 NormalY=0 NormalZ=1 AngleXU=0 Radius=1.75
    g6: Circle CenterX=14 CenterY=213.5 CenterZ=0 NormalX=0 NormalY=0 NormalZ=1 AngleXU=0 Radius=2.25
    g7: Circle CenterX=14 CenterY=221.5 CenterZ=0 NormalX=0 NormalY=0 NormalZ=1 AngleXU=0 Radius=1.75
    g8: Circle CenterX=-38 CenterY=221.5 CenterZ=0 NormalX=0 NormalY=0 NormalZ=1 AngleXU=0 Radius=2.25
  constraints (24):
    c: Coincident(g2,g1)
    c: Coincident(g2,g0)
    c: Vertical(g2)
    c: PointOnObject(g3,g-1)
    c: Vertical(g3)
    c: DistanceY(g3,g3) = 229.5
    c: DistanceY(g0) = 8
    c: Coincident(g4,g1)
    c: PointOnObject(g4,g3)
    c: Horizontal(g4)
    c: Distance(g3,g4) = 8
    c: DistanceX(g0) = 14
    c: Equal(g5,g0)
    c: Diameter(g1) = 6
    c: Diameter(g0) = 3.5
    c: PointOnObject(g6,g2)
    c: Diameter(g6) = 4.5
    c: Distance(g1,g6) = 8
    c: Symmetric(g2,g2,g5)
    c: Coincident(g7,g1)
    c: Equal(g7,g5)
    c: PointOnObject(g8,g4)
    c: Equal(g6,g8)
    c: Distance(g8,g2) = 52
FEATURE [PartDesign::Pocket] Pocket013
  BaseFeature = -> Pocket011
  Direction = (0,0,-1)
  Length = 48
  Length2 = 5
  Profile = -> Sketch044 [Edge2]
  ReferenceAxis = -> Sketch044 [N_Axis]
  Refine = true
  Reversed = true
  Suppressed = false
  Type = 0
FEATURE [PartDesign::Pocket] Pocket014
  BaseFeature = -> Pocket013
  Direction = (0,0,-1)
  Length = 5
  Length2 = 5
  Profile = -> Sketch044 [Edge5]
  ReferenceAxis = -> Sketch044 [N_Axis]
  Refine = true
  Reversed = true
  Suppressed = false
  Type = 1
FEATURE [PartDesign::Pocket] Pocket015
  BaseFeature = -> Pocket014
  Direction = (0,0,-1)
  Length = 7
  Length2 = 5
  Profile = -> Sketch044 [Edge4]
  ReferenceAxis = -> Sketch044 [N_Axis]
  Refine = true
  Reversed = true
  Suppressed = false
  Type = 0
  expr: Length = <<components>>.m3_insert_depth
FEATURE [PartDesign::Pocket] Pocket016
  BaseFeature = -> Pocket015
  Direction = (0,0,-1)
  Length = 10
  Length2 = 5
  Profile = -> Sketch044 [Edge3,Edge1]
  ReferenceAxis = -> Sketch044 [N_Axis]
  Refine = true
  Reversed = true
  Suppressed = false
  Type = 0
FEATURE [PartDesign::Plane] DatumPlane005
  AttachmentOffset = pos=(0,0,1) rot=(0,0,1;0rad)
  AttachmentSupport = -> [XY_Plane015]
  Length = 97.8846
  MapMode = 5
  Placement = pos=(0,0,1) rot=(0,0,1;0rad)
  ResizeMode = 0
  Width = 281.385
FEATURE [Sketcher::SketchObject] Sketch047  label="bottom plate screwholes001"
  ArcFitTolerance = 1e-06
  AttachmentSupport = -> [DatumPlane005]
  FullyConstrained = false
  MakeInternals = false
  MapMode = 5
  Placement = pos=(0,0,1) rot=(0,0,1;0rad)
  expr: Constraints[10] = <<choices>>.screwhole_edge_margin + 3
  expr: Constraints[11] = <<choices>>.exit_w - <<choices>>.screwhole_edge_margin
  expr: Constraints[16] = <<components>>.m3_insert_r
  expr: Constraints[5] = <<components>>.frame_h
  expr: Constraints[6] = <<choices>>.screwhole_edge_margin + 3
  sketch-geometry (8):
    g0: Circle CenterX=14 CenterY=8 CenterZ=0 NormalX=0 NormalY=0 NormalZ=1 AngleXU=0 Radius=2.75
    g1: Circle [constr] CenterX=14 CenterY=221.5 CenterZ=0 NormalX=0 NormalY=0 NormalZ=1 AngleXU=0 Radius=3
    g2: LineSegment [constr] StartX=14 StartY=221.5 StartZ=0 EndX=14 EndY=8 EndZ=0
    g3: LineSegment [constr] StartX=-60.7131 StartY=0 StartZ=0 EndX=-60.7131 EndY=229.5 EndZ=0
    g4: LineSegment [constr] StartX=14 StartY=221.5 StartZ=0 EndX=-60.7131 EndY=221.5 EndZ=0
    g5: Circle CenterX=14 CenterY=114.75 CenterZ=0 NormalX=0 NormalY=0 NormalZ=1 AngleXU=0 Radius=2.75
    g6: Circle [constr] CenterX=14 CenterY=213.5 CenterZ=0 NormalX=0 NormalY=0 NormalZ=1 AngleXU=0 Radius=2.25
    g7: Circle [constr] CenterX=14 CenterY=221.5 CenterZ=0 NormalX=0 NormalY=0 NormalZ=1 AngleXU=0 Radius=2.75
  constraints (21):
    c: Coincident(g2,g1)
    c: Coincident(g2,g0)
    c: Vertical(g2)
    c: PointOnObject(g3,g-1)
    c: Vertical(g3)
    c: DistanceY(g3,g3) = 229.5
    c: DistanceY(g0) = 8
    c: Coincident(g4,g1)
    c: PointOnObject(g4,g3)
    c: Horizontal(g4)
    c: Distance(g3,g4) = 8
    c: DistanceX(g0) = 14
    c: Equal(g5,g0)
    c: Diameter(g1) = 6
    c: Diameter(g0) = 5.5
    c: PointOnObject(g6,g2)
    c: Diameter(g6) = 4.5
    c: Distance(g1,g6) = 8
    c: Symmetric(g2,g2,g5)
    c: Coincident(g7,g1)
    c: Equal(g7,g5)
FEATURE [PartDesign::Pocket] Pocket017
  BaseFeature = -> Pocket016
  Direction = (0,0,-1)
  Length = 4
  Length2 = 5
  Profile = -> Sketch047
  ReferenceAxis = -> Sketch047 [N_Axis]
  Refine = true
  Reversed = true
  Suppressed = false
  Type = 0
FEATURE [PartDesign::Plane] DatumPlane006
  AttachmentOffset = pos=(0,0,27.5) rot=(0,0,1;0rad)
  AttachmentSupport = -> [XY_Plane015]
  Length = 97.8846
  MapMode = 5
  Placement = pos=(0,0,27.5) rot=(0,0,1;0rad)
  ResizeMode = 0
  Width = 281.385
  expr: .AttachmentOffset.Base.z = <<choices>>.exit_height / 2
FEATURE [PartDesign::Mirrored] Mirrored
  BaseFeature = -> Pocket017
  MirrorPlane = -> DatumPlane006
  Originals = -> [Pocket016,Pocket017]
  Refine = true
  Suppressed = false
  TransformMode = 0
FEATURE [PartDesign::Pocket] Pocket038
  BaseFeature = -> Mirrored
  Direction = (-1,0,0)
  Length = 5
  Length2 = 5
  Profile = -> Sketch028
  ReferenceAxis = -> Sketch028 [N_Axis]
  Refine = true
  Suppressed = false
  Type = 1
FEATURE [Sketcher::SketchObject] Sketch089
  ArcFitTolerance = 1e-06
  AttachmentSupport = -> [YZ_Plane015]
  FullyConstrained = true
  MakeInternals = false
  MapMode = 5
  Placement = pos=(0,0,0) rot=(0.57735,0.57735,0.57735;2.0944rad)
  sketch-geometry (8):
    g0: LineSegment StartX=229.5 StartY=19 StartZ=0 EndX=229.5 EndY=21.3 EndZ=0
    g1: LineSegment StartX=226.8 StartY=24 StartZ=0 EndX=226.2 EndY=24 EndZ=0
    g2: LineSegment StartX=223.5 StartY=21.3 StartZ=0 EndX=223.5 EndY=19 EndZ=0
    g3: LineSegment StartX=223.5 StartY=19 StartZ=0 EndX=229.5 EndY=19 EndZ=0
    g4: ArcOfCircle CenterX=226.8 CenterY=21.3 CenterZ=0 NormalX=0 NormalY=0 NormalZ=1 AngleXU=0 Radius=2.7 StartAngle=0 EndAngle=1.5708
    g5: GeomPoint [constr] X=229.5 Y=24 Z=0
    g6: ArcOfCircle CenterX=226.2 CenterY=21.3 CenterZ=0 NormalX=0 NormalY=0 NormalZ=1 AngleXU=0 Radius=2.7 StartAngle=1.5708 EndAngle=3.14159
    g7: GeomPoint [constr] X=223.5 Y=24 Z=0
  constraints (20):
    c: Coincident(g2,g3)
    c: Coincident(g3,g0)
    c: Vertical(g0)
    c: Vertical(g2)
    c: Horizontal(g1)
    c: Horizontal(g3)
    c: DistanceX(g0) = 229.5
    c: DistanceY(g0) = 19
    c: PointOnObject(g5,g0)
    c: PointOnObject(g5,g1)
    c: Tangent(g0,g4) = -1.5708
    c: Tangent(g1,g4) = -1.5708
    c: PointOnObject(g7,g1)
    c: PointOnObject(g7,g2)
    c: Tangent(g1,g6) = -1.5708
    c: Tangent(g2,g6) = -1.5708
    c: Equal(g4,g6)
    c: DistanceY(g1) = 24
    c: DistanceY(g0) = 21.3
    c: DistanceX(g3,g3) = 6
FEATURE [PartDesign::Pad] Pad046
  BaseFeature = -> Pocket038
  Direction = (1,0,0)
  Length = 30
  Length2 = 10
  Midplane = true
  Profile = -> Sketch089
  ReferenceAxis = -> Sketch089 [N_Axis]
  Refine = true
  Suppressed = false
  TaperAngle = -9
  Type = 0
FEATURE [Sketcher::SketchObject] Sketch090
  ArcFitTolerance = 1e-06
  AttachmentSupport = -> [DatumPlane003]
  FullyConstrained = false
  MakeInternals = false
  MapMode = 5
  Placement = pos=(-25,0,0) rot=(0.57735,0.57735,0.57735;2.0944rad)
  expr: Constraints[6] = <<components>>.frame_h
  sketch-geometry (8):
    g0: LineSegment StartX=229.5 StartY=31.8586 StartZ=0 EndX=223.5 EndY=31.8586 EndZ=0
    g1: LineSegment StartX=223.5 StartY=31.8586 StartZ=0 EndX=223.5 EndY=28.7 EndZ=0
    g2: LineSegment StartX=226.2 StartY=26 StartZ=0 EndX=226.8 EndY=26 EndZ=0
    g3: LineSegment StartX=229.5 StartY=28.7 StartZ=0 EndX=229.5 EndY=31.8586 EndZ=0
    g4: ArcOfCircle CenterX=226.8 CenterY=28.7 CenterZ=0 NormalX=0 NormalY=0 NormalZ=1 AngleXU=0 Radius=2.7 StartAngle=4.71239 EndAngle=6.28319
    g5: GeomPoint [constr] X=229.5 Y=26 Z=0
    g6: ArcOfCircle CenterX=226.2 CenterY=28.7 CenterZ=0 NormalX=0 NormalY=0 NormalZ=1 AngleXU=0 Radius=2.7 StartAngle=3.14159 EndAngle=4.71239
    g7: GeomPoint [constr] X=223.5 Y=26 Z=0
  constraints (19):
    c: Coincident(g0,g1)
    c: Coincident(g3,g0)
    c: Horizontal(g0)
    c: Horizontal(g2)
    c: Vertical(g1)
    c: Vertical(g3)
    c: DistanceX(g0) = 229.5
    c: DistanceY(g5) = 26
    c: PointOnObject(g5,g2)
    c: PointOnObject(g5,g3)
    c: Tangent(g2,g4) = -1.5708
    c: Tangent(g3,g4) = -1.5708
    c: PointOnObject(g7,g1)
    c: PointOnObject(g7,g2)
    c: Tangent(g1,g6) = -1.5708
    c: Tangent(g2,g6) = -1.5708
    c: Equal(g6,g4)
    c: DistanceY(g3) = 28.7
    c: DistanceX(g0,g0) = 6
FEATURE [PartDesign::Pad] Pad047
  BaseFeature = -> Pad046
  Direction = (1,0,0)
  Length = 30
  Length2 = 10
  Midplane = true
  Profile = -> Sketch090
  ReferenceAxis = -> Sketch090 [N_Axis]
  Refine = true
  Suppressed = false
  TaperAngle = -9
  Type = 0
FEATURE [PartDesign::Body] Body007
  AllowCompound = false
  Group = -> [Sketch015,Pad012,Pad021,Pad023,Fillet,Sketch022,Pocket008,DatumPlane002,Sketch023,Sketch024,Sketch025,SubtractiveLoft,Sketch026,Sketch027,AdditiveLoft,LinearPattern001,Sketch028,Sketch036,DatumPlane003,DatumPlane004,Sketch041,Pocket011,Sketch043,Sketch044,Pocket013,Pocket014,Pocket015,Pocket016,DatumPlane005,Sketch047,Pocket017,DatumPlane006,Mirrored,Pocket038,Sketch089,Pad046,Sketch090,Pad047,+6 more]
  Origin = -> Origin015
  Tip = -> Fillet002
